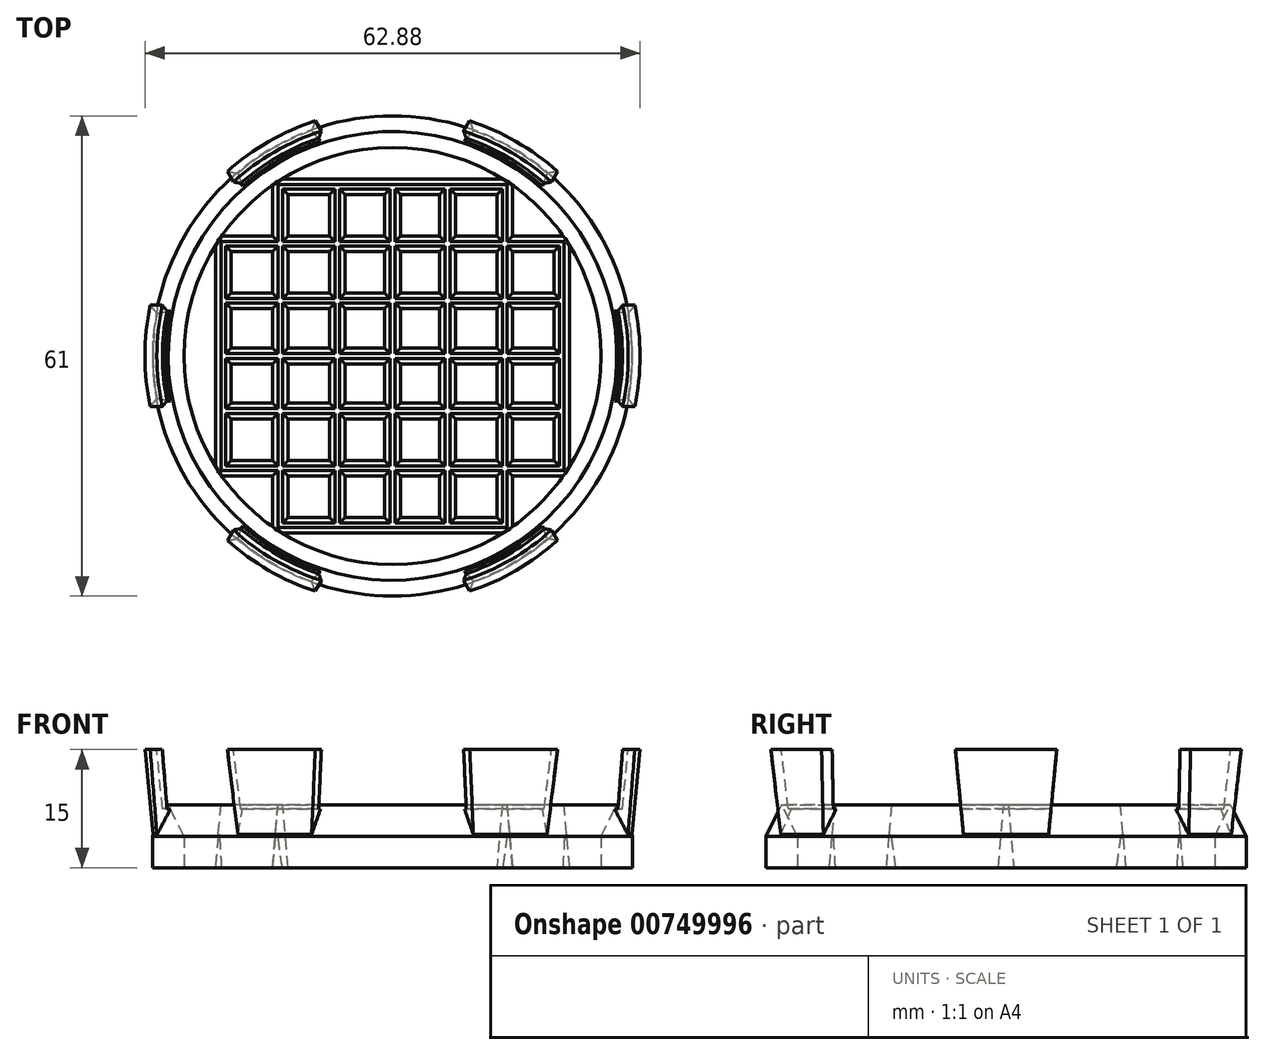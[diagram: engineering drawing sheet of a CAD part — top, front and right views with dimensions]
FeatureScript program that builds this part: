
annotation { "Feature Type Name" : "Feature", "Feature Type Description" : "" }
export const myFeature = defineFeature(function(context is Context, id is Id, definition is map)
    precondition{}
    {
        {
            var Q0;
            Q0=qCreatedBy(makeId("Front.planeOp"),FACE);
            var sketch = newSketch(context, id + "F0", { "sketchPlane" : qUnion([Q0])});
            skLineSegment(sketch, "E0", {"start": v(26.5, 0) * mm, "end": v(26.5, 4) * mm});
            skLineSegment(sketch, "E1", {"start": v(26.5, 4) * mm, "end": v(28.5, 8) * mm});
            skLineSegment(sketch, "E2", {"start": v(28.5, 8) * mm, "end": v(30.5, 4) * mm});
            skLineSegment(sketch, "E3", {"start": v(30.5, 4) * mm, "end": v(30.5, 0) * mm});
            skLineSegment(sketch, "E4", {"start": v(30.5, 0) * mm, "end": v(26.5, 0) * mm});
            skLineSegment(sketch, "E5", {"start": v(0, 0) * mm, "end": v(0, 8.18) * mm, "construction": true});
            skPoint(sketch, "E6", {"position": v(28.5, 0) * mm});
            skSolve(sketch);
        }
        {
            var Q0;
            Q0=makeQuery(id+"F0.imprint","IMPRINT",FACE,{"disambiguationData":[TD([[makeQuery(id+"F0.imprint","IMPRINT",EDGE,{"derivedFrom":sQuery(id+"F0.wireOp",EDGE,"E0")}),-1.0]])]});
            var Q1;
            Q1=sQuery(id+"F0.wireOp",EDGE,"E5");
            revolve(context, id + "F1", {"surfaceOperationType" : NewSurfaceOperationType.NEW, "entities" : qUnion([Q0]), "axis" : qUnion([Q1]), "revolveType" : RevolveType.FULL});
        }
        {
            var Q0;
            Q0=qCreatedBy(makeId("Top.planeOp"),FACE);
            var sketch = newSketch(context, id + "F2", { "sketchPlane" : qUnion([Q0])});
            skCircle(sketch, "E7.0", {"center": v(0, 0) * mm, "radius": 28.5 * mm});
            skLineSegment(sketch, "E8", {"start": v(-28.48, 1) * mm, "end": v(28.48, 1) * mm});
            skLineSegment(sketch, "E9", {"start": v(-28.48, -1) * mm, "end": v(28.48, -1) * mm});
            skLineSegment(sketch, "E10.0", {"start": v(-27.86, 6) * mm, "end": v(27.86, 6) * mm});
            skLineSegment(sketch, "E11.0", {"start": v(-27.35, 8) * mm, "end": v(27.35, 8) * mm});
            skLineSegment(sketch, "E12.0", {"start": v(-25.23, 13.25) * mm, "end": v(25.23, 13.25) * mm});
            skLineSegment(sketch, "E13.0", {"start": v(-24.08, 15.25) * mm, "end": v(24.08, 15.25) * mm});
            skLineSegment(sketch, "E14.0", {"start": v(-19.8, 20.5) * mm, "end": v(19.8, 20.5) * mm});
            skLineSegment(sketch, "E15.0", {"start": v(-17.5, 22.5) * mm, "end": v(17.5, 22.5) * mm});
            skLineSegment(sketch, "E16.0", {"start": v(-27.86, -6) * mm, "end": v(27.86, -6) * mm});
            skLineSegment(sketch, "E17.0", {"start": v(-27.35, -8) * mm, "end": v(27.35, -8) * mm});
            skLineSegment(sketch, "E18.0", {"start": v(-25.23, -13.25) * mm, "end": v(25.23, -13.25) * mm});
            skLineSegment(sketch, "E19.0", {"start": v(-24.08, -15.25) * mm, "end": v(24.08, -15.25) * mm});
            skLineSegment(sketch, "E20.0", {"start": v(-19.8, -20.5) * mm, "end": v(19.8, -20.5) * mm});
            skLineSegment(sketch, "E21.0", {"start": v(-17.5, -22.5) * mm, "end": v(17.5, -22.5) * mm});
            skLineSegment(sketch, "E22", {"start": v(-1, 28.48) * mm, "end": v(-1, -28.48) * mm});
            skLineSegment(sketch, "E23", {"start": v(1, 28.48) * mm, "end": v(1, -28.48) * mm});
            skLineSegment(sketch, "E24.0", {"start": v(-6, 27.86) * mm, "end": v(-6, -27.86) * mm});
            skLineSegment(sketch, "E25.0", {"start": v(-8, 27.35) * mm, "end": v(-8, -27.35) * mm});
            skLineSegment(sketch, "E26.0", {"start": v(-13.25, 25.23) * mm, "end": v(-13.25, -25.23) * mm});
            skLineSegment(sketch, "E27.0", {"start": v(-15.25, 24.08) * mm, "end": v(-15.25, -24.08) * mm});
            skLineSegment(sketch, "E28.0", {"start": v(-20.5, 19.8) * mm, "end": v(-20.5, -19.8) * mm});
            skLineSegment(sketch, "E29.0", {"start": v(-22.5, 17.5) * mm, "end": v(-22.5, -17.5) * mm});
            skLineSegment(sketch, "E30.0", {"start": v(8, 27.35) * mm, "end": v(8, -27.35) * mm});
            skLineSegment(sketch, "E31.0", {"start": v(6, 27.86) * mm, "end": v(6, -27.86) * mm});
            skLineSegment(sketch, "E32.0", {"start": v(13.25, 25.23) * mm, "end": v(13.25, -25.23) * mm});
            skLineSegment(sketch, "E33.0", {"start": v(15.25, 24.08) * mm, "end": v(15.25, -24.08) * mm});
            skLineSegment(sketch, "E34.0", {"start": v(20.5, 19.8) * mm, "end": v(20.5, -19.8) * mm});
            skLineSegment(sketch, "E35.0", {"start": v(22.5, 17.5) * mm, "end": v(22.5, -17.5) * mm});
            skSolve(sketch);
        }
        {
            var Q0;
            {var subQ0=sQuery(id+"F2.wireOp",EDGE,"E26.0");var subQ1=sQuery(id+"F2.wireOp",EDGE,"E7.0");var subQ2=makeQuery(id+"F2.imprint","INTERSECT",VERTEX,{"disambiguationData":[OD(0.0)],"derivedFrom":[subQ1,subQ0]});Q0=makeQuery(id+"F2.imprint","IMPRINT",FACE,{"disambiguationData":[TD([[makeQuery(id+"F2.imprint","IMPRINT",EDGE,{"disambiguationData":[TD([[subQ2,1.0]])],"derivedFrom":subQ1}),-1.0]])]});}
            var Q1;
            {var subQ0=sQuery(id+"F2.wireOp",EDGE,"E24.0");var subQ1=sQuery(id+"F2.wireOp",EDGE,"E7.0");var subQ2=makeQuery(id+"F2.imprint","INTERSECT",VERTEX,{"disambiguationData":[OD(0.0)],"derivedFrom":[subQ1,subQ0]});Q1=makeQuery(id+"F2.imprint","IMPRINT",FACE,{"disambiguationData":[TD([[makeQuery(id+"F2.imprint","IMPRINT",EDGE,{"disambiguationData":[TD([[subQ2,1.0]])],"derivedFrom":subQ1}),-1.0]])]});}
            var Q2;
            {var subQ0=sQuery(id+"F2.wireOp",EDGE,"E22");var subQ1=sQuery(id+"F2.wireOp",EDGE,"E7.0");var subQ2=makeQuery(id+"F2.imprint","INTERSECT",VERTEX,{"disambiguationData":[OD(0.0)],"derivedFrom":[subQ1,subQ0]});Q2=makeQuery(id+"F2.imprint","IMPRINT",FACE,{"disambiguationData":[TD([[makeQuery(id+"F2.imprint","IMPRINT",EDGE,{"disambiguationData":[TD([[subQ2,-1.0]])],"derivedFrom":subQ1}),-1.0]])]});}
            var Q3;
            {var subQ0=sQuery(id+"F2.wireOp",EDGE,"E30.0");var subQ1=sQuery(id+"F2.wireOp",EDGE,"E7.0");var subQ2=makeQuery(id+"F2.imprint","INTERSECT",VERTEX,{"disambiguationData":[OD(0.0)],"derivedFrom":[subQ1,subQ0]});Q3=makeQuery(id+"F2.imprint","IMPRINT",FACE,{"disambiguationData":[TD([[makeQuery(id+"F2.imprint","IMPRINT",EDGE,{"disambiguationData":[TD([[subQ2,1.0]])],"derivedFrom":subQ1}),-1.0]])]});}
            var Q4;
            {var subQ0=sQuery(id+"F2.wireOp",EDGE,"E32.0");var subQ1=sQuery(id+"F2.wireOp",EDGE,"E7.0");var subQ2=makeQuery(id+"F2.imprint","INTERSECT",VERTEX,{"disambiguationData":[OD(0.0)],"derivedFrom":[subQ1,subQ0]});Q4=makeQuery(id+"F2.imprint","IMPRINT",FACE,{"disambiguationData":[TD([[makeQuery(id+"F2.imprint","IMPRINT",EDGE,{"disambiguationData":[TD([[subQ2,-1.0]])],"derivedFrom":subQ1}),-1.0]])]});}
            var Q5;
            {var subQ0=sQuery(id+"F2.wireOp",EDGE,"E14.0");var subQ1=sQuery(id+"F2.wireOp",EDGE,"E7.0");var subQ2=makeQuery(id+"F2.imprint","INTERSECT",VERTEX,{"disambiguationData":[OD(0.0)],"derivedFrom":[subQ1,subQ0]});Q5=makeQuery(id+"F2.imprint","IMPRINT",FACE,{"disambiguationData":[TD([[makeQuery(id+"F2.imprint","IMPRINT",EDGE,{"disambiguationData":[TD([[subQ2,-1.0]])],"derivedFrom":subQ1}),-1.0]])]});}
            var Q6;
            {var subQ0=sQuery(id+"F2.wireOp",EDGE,"E27.0");var subQ1=sQuery(id+"F2.wireOp",EDGE,"E14.0");var subQ2=makeQuery(id+"F2.imprint","INTERSECT",VERTEX,{"derivedFrom":[subQ1,subQ0]});Q6=makeQuery(id+"F2.imprint","IMPRINT",FACE,{"disambiguationData":[TD([[makeQuery(id+"F2.imprint","IMPRINT",EDGE,{"disambiguationData":[TD([[subQ2,-1.0]])],"derivedFrom":subQ1}),1.0]])]});}
            var Q7;
            {var subQ0=sQuery(id+"F2.wireOp",EDGE,"E26.0");var subQ1=sQuery(id+"F2.wireOp",EDGE,"E14.0");var subQ2=makeQuery(id+"F2.imprint","INTERSECT",VERTEX,{"derivedFrom":[subQ1,subQ0]});Q7=makeQuery(id+"F2.imprint","IMPRINT",FACE,{"disambiguationData":[TD([[makeQuery(id+"F2.imprint","IMPRINT",EDGE,{"disambiguationData":[TD([[subQ2,-1.0]])],"derivedFrom":subQ1}),1.0]])]});}
            var Q8;
            {var subQ0=sQuery(id+"F2.wireOp",EDGE,"E25.0");var subQ1=sQuery(id+"F2.wireOp",EDGE,"E14.0");var subQ2=makeQuery(id+"F2.imprint","INTERSECT",VERTEX,{"derivedFrom":[subQ1,subQ0]});Q8=makeQuery(id+"F2.imprint","IMPRINT",FACE,{"disambiguationData":[TD([[makeQuery(id+"F2.imprint","IMPRINT",EDGE,{"disambiguationData":[TD([[subQ2,-1.0]])],"derivedFrom":subQ1}),1.0]])]});}
            var Q9;
            {var subQ0=sQuery(id+"F2.wireOp",EDGE,"E24.0");var subQ1=sQuery(id+"F2.wireOp",EDGE,"E14.0");var subQ2=makeQuery(id+"F2.imprint","INTERSECT",VERTEX,{"derivedFrom":[subQ1,subQ0]});Q9=makeQuery(id+"F2.imprint","IMPRINT",FACE,{"disambiguationData":[TD([[makeQuery(id+"F2.imprint","IMPRINT",EDGE,{"disambiguationData":[TD([[subQ2,-1.0]])],"derivedFrom":subQ1}),1.0]])]});}
            var Q10;
            {var subQ0=sQuery(id+"F2.wireOp",EDGE,"E22");var subQ1=sQuery(id+"F2.wireOp",EDGE,"E14.0");var subQ2=makeQuery(id+"F2.imprint","INTERSECT",VERTEX,{"derivedFrom":[subQ1,subQ0]});Q10=makeQuery(id+"F2.imprint","IMPRINT",FACE,{"disambiguationData":[TD([[makeQuery(id+"F2.imprint","IMPRINT",EDGE,{"disambiguationData":[TD([[subQ2,-1.0]])],"derivedFrom":subQ1}),1.0]])]});}
            var Q11;
            {var subQ0=sQuery(id+"F2.wireOp",EDGE,"E23");var subQ1=sQuery(id+"F2.wireOp",EDGE,"E14.0");var subQ2=makeQuery(id+"F2.imprint","INTERSECT",VERTEX,{"derivedFrom":[subQ1,subQ0]});Q11=makeQuery(id+"F2.imprint","IMPRINT",FACE,{"disambiguationData":[TD([[makeQuery(id+"F2.imprint","IMPRINT",EDGE,{"disambiguationData":[TD([[subQ2,-1.0]])],"derivedFrom":subQ1}),1.0]])]});}
            var Q12;
            {var subQ0=sQuery(id+"F2.wireOp",EDGE,"E31.0");var subQ1=sQuery(id+"F2.wireOp",EDGE,"E14.0");var subQ2=makeQuery(id+"F2.imprint","INTERSECT",VERTEX,{"derivedFrom":[subQ1,subQ0]});Q12=makeQuery(id+"F2.imprint","IMPRINT",FACE,{"disambiguationData":[TD([[makeQuery(id+"F2.imprint","IMPRINT",EDGE,{"disambiguationData":[TD([[subQ2,-1.0]])],"derivedFrom":subQ1}),1.0]])]});}
            var Q13;
            {var subQ0=sQuery(id+"F2.wireOp",EDGE,"E30.0");var subQ1=sQuery(id+"F2.wireOp",EDGE,"E14.0");var subQ2=makeQuery(id+"F2.imprint","INTERSECT",VERTEX,{"derivedFrom":[subQ1,subQ0]});Q13=makeQuery(id+"F2.imprint","IMPRINT",FACE,{"disambiguationData":[TD([[makeQuery(id+"F2.imprint","IMPRINT",EDGE,{"disambiguationData":[TD([[subQ2,-1.0]])],"derivedFrom":subQ1}),1.0]])]});}
            var Q14;
            {var subQ0=sQuery(id+"F2.wireOp",EDGE,"E32.0");var subQ1=sQuery(id+"F2.wireOp",EDGE,"E14.0");var subQ2=makeQuery(id+"F2.imprint","INTERSECT",VERTEX,{"derivedFrom":[subQ1,subQ0]});Q14=makeQuery(id+"F2.imprint","IMPRINT",FACE,{"disambiguationData":[TD([[makeQuery(id+"F2.imprint","IMPRINT",EDGE,{"disambiguationData":[TD([[subQ2,-1.0]])],"derivedFrom":subQ1}),1.0]])]});}
            var Q15;
            {var subQ0=sQuery(id+"F2.wireOp",EDGE,"E14.0");var subQ1=sQuery(id+"F2.wireOp",EDGE,"E7.0");var subQ2=makeQuery(id+"F2.imprint","INTERSECT",VERTEX,{"disambiguationData":[OD(1.0)],"derivedFrom":[subQ1,subQ0]});Q15=makeQuery(id+"F2.imprint","IMPRINT",FACE,{"disambiguationData":[TD([[makeQuery(id+"F2.imprint","IMPRINT",EDGE,{"disambiguationData":[TD([[subQ2,1.0]])],"derivedFrom":subQ1}),-1.0]])]});}
            var Q16;
            {var subQ0=sQuery(id+"F2.wireOp",EDGE,"E28.0");var subQ1=sQuery(id+"F2.wireOp",EDGE,"E7.0");var subQ2=makeQuery(id+"F2.imprint","INTERSECT",VERTEX,{"disambiguationData":[OD(0.0)],"derivedFrom":[subQ1,subQ0]});Q16=makeQuery(id+"F2.imprint","IMPRINT",FACE,{"disambiguationData":[TD([[makeQuery(id+"F2.imprint","IMPRINT",EDGE,{"disambiguationData":[TD([[subQ2,1.0]])],"derivedFrom":subQ1}),-1.0]])]});}
            var Q17;
            {var subQ0=sQuery(id+"F2.wireOp",EDGE,"E27.0");var subQ1=sQuery(id+"F2.wireOp",EDGE,"E13.0");var subQ2=makeQuery(id+"F2.imprint","INTERSECT",VERTEX,{"derivedFrom":[subQ1,subQ0]});Q17=makeQuery(id+"F2.imprint","IMPRINT",FACE,{"disambiguationData":[TD([[makeQuery(id+"F2.imprint","IMPRINT",EDGE,{"disambiguationData":[TD([[subQ2,-1.0]])],"derivedFrom":subQ1}),1.0]])]});}
            var Q18;
            {var subQ0=sQuery(id+"F2.wireOp",EDGE,"E25.0");var subQ1=sQuery(id+"F2.wireOp",EDGE,"E13.0");var subQ2=makeQuery(id+"F2.imprint","INTERSECT",VERTEX,{"derivedFrom":[subQ1,subQ0]});Q18=makeQuery(id+"F2.imprint","IMPRINT",FACE,{"disambiguationData":[TD([[makeQuery(id+"F2.imprint","IMPRINT",EDGE,{"disambiguationData":[TD([[subQ2,-1.0]])],"derivedFrom":subQ1}),1.0]])]});}
            var Q19;
            {var subQ0=sQuery(id+"F2.wireOp",EDGE,"E22");var subQ1=sQuery(id+"F2.wireOp",EDGE,"E13.0");var subQ2=makeQuery(id+"F2.imprint","INTERSECT",VERTEX,{"derivedFrom":[subQ1,subQ0]});Q19=makeQuery(id+"F2.imprint","IMPRINT",FACE,{"disambiguationData":[TD([[makeQuery(id+"F2.imprint","IMPRINT",EDGE,{"disambiguationData":[TD([[subQ2,-1.0]])],"derivedFrom":subQ1}),1.0]])]});}
            var Q20;
            {var subQ0=sQuery(id+"F2.wireOp",EDGE,"E31.0");var subQ1=sQuery(id+"F2.wireOp",EDGE,"E13.0");var subQ2=makeQuery(id+"F2.imprint","INTERSECT",VERTEX,{"derivedFrom":[subQ1,subQ0]});Q20=makeQuery(id+"F2.imprint","IMPRINT",FACE,{"disambiguationData":[TD([[makeQuery(id+"F2.imprint","IMPRINT",EDGE,{"disambiguationData":[TD([[subQ2,-1.0]])],"derivedFrom":subQ1}),1.0]])]});}
            var Q21;
            {var subQ0=sQuery(id+"F2.wireOp",EDGE,"E32.0");var subQ1=sQuery(id+"F2.wireOp",EDGE,"E13.0");var subQ2=makeQuery(id+"F2.imprint","INTERSECT",VERTEX,{"derivedFrom":[subQ1,subQ0]});Q21=makeQuery(id+"F2.imprint","IMPRINT",FACE,{"disambiguationData":[TD([[makeQuery(id+"F2.imprint","IMPRINT",EDGE,{"disambiguationData":[TD([[subQ2,-1.0]])],"derivedFrom":subQ1}),1.0]])]});}
            var Q22;
            {var subQ0=sQuery(id+"F2.wireOp",EDGE,"E34.0");var subQ1=sQuery(id+"F2.wireOp",EDGE,"E7.0");var subQ2=makeQuery(id+"F2.imprint","INTERSECT",VERTEX,{"disambiguationData":[OD(0.0)],"derivedFrom":[subQ1,subQ0]});Q22=makeQuery(id+"F2.imprint","IMPRINT",FACE,{"disambiguationData":[TD([[makeQuery(id+"F2.imprint","IMPRINT",EDGE,{"disambiguationData":[TD([[subQ2,-1.0]])],"derivedFrom":subQ1}),-1.0]])]});}
            var Q23;
            {var subQ0=sQuery(id+"F2.wireOp",EDGE,"E12.0");var subQ1=sQuery(id+"F2.wireOp",EDGE,"E7.0");var subQ2=makeQuery(id+"F2.imprint","INTERSECT",VERTEX,{"disambiguationData":[OD(0.0)],"derivedFrom":[subQ1,subQ0]});Q23=makeQuery(id+"F2.imprint","IMPRINT",FACE,{"disambiguationData":[TD([[makeQuery(id+"F2.imprint","IMPRINT",EDGE,{"disambiguationData":[TD([[subQ2,-1.0]])],"derivedFrom":subQ1}),-1.0]])]});}
            var Q24;
            {var subQ0=sQuery(id+"F2.wireOp",EDGE,"E29.0");var subQ1=sQuery(id+"F2.wireOp",EDGE,"E12.0");var subQ2=makeQuery(id+"F2.imprint","INTERSECT",VERTEX,{"derivedFrom":[subQ1,subQ0]});Q24=makeQuery(id+"F2.imprint","IMPRINT",FACE,{"disambiguationData":[TD([[makeQuery(id+"F2.imprint","IMPRINT",EDGE,{"disambiguationData":[TD([[subQ2,-1.0]])],"derivedFrom":subQ1}),1.0]])]});}
            var Q25;
            {var subQ0=sQuery(id+"F2.wireOp",EDGE,"E28.0");var subQ1=sQuery(id+"F2.wireOp",EDGE,"E12.0");var subQ2=makeQuery(id+"F2.imprint","INTERSECT",VERTEX,{"derivedFrom":[subQ1,subQ0]});Q25=makeQuery(id+"F2.imprint","IMPRINT",FACE,{"disambiguationData":[TD([[makeQuery(id+"F2.imprint","IMPRINT",EDGE,{"disambiguationData":[TD([[subQ2,-1.0]])],"derivedFrom":subQ1}),1.0]])]});}
            var Q26;
            {var subQ0=sQuery(id+"F2.wireOp",EDGE,"E27.0");var subQ1=sQuery(id+"F2.wireOp",EDGE,"E12.0");var subQ2=makeQuery(id+"F2.imprint","INTERSECT",VERTEX,{"derivedFrom":[subQ1,subQ0]});Q26=makeQuery(id+"F2.imprint","IMPRINT",FACE,{"disambiguationData":[TD([[makeQuery(id+"F2.imprint","IMPRINT",EDGE,{"disambiguationData":[TD([[subQ2,-1.0]])],"derivedFrom":subQ1}),1.0]])]});}
            var Q27;
            {var subQ0=sQuery(id+"F2.wireOp",EDGE,"E26.0");var subQ1=sQuery(id+"F2.wireOp",EDGE,"E12.0");var subQ2=makeQuery(id+"F2.imprint","INTERSECT",VERTEX,{"derivedFrom":[subQ1,subQ0]});Q27=makeQuery(id+"F2.imprint","IMPRINT",FACE,{"disambiguationData":[TD([[makeQuery(id+"F2.imprint","IMPRINT",EDGE,{"disambiguationData":[TD([[subQ2,-1.0]])],"derivedFrom":subQ1}),1.0]])]});}
            var Q28;
            {var subQ0=sQuery(id+"F2.wireOp",EDGE,"E25.0");var subQ1=sQuery(id+"F2.wireOp",EDGE,"E12.0");var subQ2=makeQuery(id+"F2.imprint","INTERSECT",VERTEX,{"derivedFrom":[subQ1,subQ0]});Q28=makeQuery(id+"F2.imprint","IMPRINT",FACE,{"disambiguationData":[TD([[makeQuery(id+"F2.imprint","IMPRINT",EDGE,{"disambiguationData":[TD([[subQ2,-1.0]])],"derivedFrom":subQ1}),1.0]])]});}
            var Q29;
            {var subQ0=sQuery(id+"F2.wireOp",EDGE,"E24.0");var subQ1=sQuery(id+"F2.wireOp",EDGE,"E12.0");var subQ2=makeQuery(id+"F2.imprint","INTERSECT",VERTEX,{"derivedFrom":[subQ1,subQ0]});Q29=makeQuery(id+"F2.imprint","IMPRINT",FACE,{"disambiguationData":[TD([[makeQuery(id+"F2.imprint","IMPRINT",EDGE,{"disambiguationData":[TD([[subQ2,-1.0]])],"derivedFrom":subQ1}),1.0]])]});}
            var Q30;
            {var subQ0=sQuery(id+"F2.wireOp",EDGE,"E22");var subQ1=sQuery(id+"F2.wireOp",EDGE,"E12.0");var subQ2=makeQuery(id+"F2.imprint","INTERSECT",VERTEX,{"derivedFrom":[subQ1,subQ0]});Q30=makeQuery(id+"F2.imprint","IMPRINT",FACE,{"disambiguationData":[TD([[makeQuery(id+"F2.imprint","IMPRINT",EDGE,{"disambiguationData":[TD([[subQ2,-1.0]])],"derivedFrom":subQ1}),1.0]])]});}
            var Q31;
            {var subQ0=sQuery(id+"F2.wireOp",EDGE,"E23");var subQ1=sQuery(id+"F2.wireOp",EDGE,"E12.0");var subQ2=makeQuery(id+"F2.imprint","INTERSECT",VERTEX,{"derivedFrom":[subQ1,subQ0]});Q31=makeQuery(id+"F2.imprint","IMPRINT",FACE,{"disambiguationData":[TD([[makeQuery(id+"F2.imprint","IMPRINT",EDGE,{"disambiguationData":[TD([[subQ2,-1.0]])],"derivedFrom":subQ1}),1.0]])]});}
            var Q32;
            {var subQ0=sQuery(id+"F2.wireOp",EDGE,"E31.0");var subQ1=sQuery(id+"F2.wireOp",EDGE,"E12.0");var subQ2=makeQuery(id+"F2.imprint","INTERSECT",VERTEX,{"derivedFrom":[subQ1,subQ0]});Q32=makeQuery(id+"F2.imprint","IMPRINT",FACE,{"disambiguationData":[TD([[makeQuery(id+"F2.imprint","IMPRINT",EDGE,{"disambiguationData":[TD([[subQ2,-1.0]])],"derivedFrom":subQ1}),1.0]])]});}
            var Q33;
            {var subQ0=sQuery(id+"F2.wireOp",EDGE,"E30.0");var subQ1=sQuery(id+"F2.wireOp",EDGE,"E12.0");var subQ2=makeQuery(id+"F2.imprint","INTERSECT",VERTEX,{"derivedFrom":[subQ1,subQ0]});Q33=makeQuery(id+"F2.imprint","IMPRINT",FACE,{"disambiguationData":[TD([[makeQuery(id+"F2.imprint","IMPRINT",EDGE,{"disambiguationData":[TD([[subQ2,-1.0]])],"derivedFrom":subQ1}),1.0]])]});}
            var Q34;
            {var subQ0=sQuery(id+"F2.wireOp",EDGE,"E32.0");var subQ1=sQuery(id+"F2.wireOp",EDGE,"E12.0");var subQ2=makeQuery(id+"F2.imprint","INTERSECT",VERTEX,{"derivedFrom":[subQ1,subQ0]});Q34=makeQuery(id+"F2.imprint","IMPRINT",FACE,{"disambiguationData":[TD([[makeQuery(id+"F2.imprint","IMPRINT",EDGE,{"disambiguationData":[TD([[subQ2,-1.0]])],"derivedFrom":subQ1}),1.0]])]});}
            var Q35;
            {var subQ0=sQuery(id+"F2.wireOp",EDGE,"E33.0");var subQ1=sQuery(id+"F2.wireOp",EDGE,"E12.0");var subQ2=makeQuery(id+"F2.imprint","INTERSECT",VERTEX,{"derivedFrom":[subQ1,subQ0]});Q35=makeQuery(id+"F2.imprint","IMPRINT",FACE,{"disambiguationData":[TD([[makeQuery(id+"F2.imprint","IMPRINT",EDGE,{"disambiguationData":[TD([[subQ2,-1.0]])],"derivedFrom":subQ1}),1.0]])]});}
            var Q36;
            {var subQ0=sQuery(id+"F2.wireOp",EDGE,"E34.0");var subQ1=sQuery(id+"F2.wireOp",EDGE,"E12.0");var subQ2=makeQuery(id+"F2.imprint","INTERSECT",VERTEX,{"derivedFrom":[subQ1,subQ0]});Q36=makeQuery(id+"F2.imprint","IMPRINT",FACE,{"disambiguationData":[TD([[makeQuery(id+"F2.imprint","IMPRINT",EDGE,{"disambiguationData":[TD([[subQ2,-1.0]])],"derivedFrom":subQ1}),1.0]])]});}
            var Q37;
            {var subQ0=sQuery(id+"F2.wireOp",EDGE,"E12.0");var subQ1=sQuery(id+"F2.wireOp",EDGE,"E7.0");var subQ2=makeQuery(id+"F2.imprint","INTERSECT",VERTEX,{"disambiguationData":[OD(1.0)],"derivedFrom":[subQ1,subQ0]});Q37=makeQuery(id+"F2.imprint","IMPRINT",FACE,{"disambiguationData":[TD([[makeQuery(id+"F2.imprint","IMPRINT",EDGE,{"disambiguationData":[TD([[subQ2,1.0]])],"derivedFrom":subQ1}),-1.0]])]});}
            var Q38;
            {var subQ0=sQuery(id+"F2.wireOp",EDGE,"E29.0");var subQ1=sQuery(id+"F2.wireOp",EDGE,"E11.0");var subQ2=makeQuery(id+"F2.imprint","INTERSECT",VERTEX,{"derivedFrom":[subQ1,subQ0]});Q38=makeQuery(id+"F2.imprint","IMPRINT",FACE,{"disambiguationData":[TD([[makeQuery(id+"F2.imprint","IMPRINT",EDGE,{"disambiguationData":[TD([[subQ2,-1.0]])],"derivedFrom":subQ1}),1.0]])]});}
            var Q39;
            {var subQ0=sQuery(id+"F2.wireOp",EDGE,"E27.0");var subQ1=sQuery(id+"F2.wireOp",EDGE,"E11.0");var subQ2=makeQuery(id+"F2.imprint","INTERSECT",VERTEX,{"derivedFrom":[subQ1,subQ0]});Q39=makeQuery(id+"F2.imprint","IMPRINT",FACE,{"disambiguationData":[TD([[makeQuery(id+"F2.imprint","IMPRINT",EDGE,{"disambiguationData":[TD([[subQ2,-1.0]])],"derivedFrom":subQ1}),1.0]])]});}
            var Q40;
            {var subQ0=sQuery(id+"F2.wireOp",EDGE,"E25.0");var subQ1=sQuery(id+"F2.wireOp",EDGE,"E11.0");var subQ2=makeQuery(id+"F2.imprint","INTERSECT",VERTEX,{"derivedFrom":[subQ1,subQ0]});Q40=makeQuery(id+"F2.imprint","IMPRINT",FACE,{"disambiguationData":[TD([[makeQuery(id+"F2.imprint","IMPRINT",EDGE,{"disambiguationData":[TD([[subQ2,-1.0]])],"derivedFrom":subQ1}),1.0]])]});}
            var Q41;
            {var subQ0=sQuery(id+"F2.wireOp",EDGE,"E22");var subQ1=sQuery(id+"F2.wireOp",EDGE,"E11.0");var subQ2=makeQuery(id+"F2.imprint","INTERSECT",VERTEX,{"derivedFrom":[subQ1,subQ0]});Q41=makeQuery(id+"F2.imprint","IMPRINT",FACE,{"disambiguationData":[TD([[makeQuery(id+"F2.imprint","IMPRINT",EDGE,{"disambiguationData":[TD([[subQ2,-1.0]])],"derivedFrom":subQ1}),1.0]])]});}
            var Q42;
            {var subQ0=sQuery(id+"F2.wireOp",EDGE,"E31.0");var subQ1=sQuery(id+"F2.wireOp",EDGE,"E11.0");var subQ2=makeQuery(id+"F2.imprint","INTERSECT",VERTEX,{"derivedFrom":[subQ1,subQ0]});Q42=makeQuery(id+"F2.imprint","IMPRINT",FACE,{"disambiguationData":[TD([[makeQuery(id+"F2.imprint","IMPRINT",EDGE,{"disambiguationData":[TD([[subQ2,-1.0]])],"derivedFrom":subQ1}),1.0]])]});}
            var Q43;
            {var subQ0=sQuery(id+"F2.wireOp",EDGE,"E32.0");var subQ1=sQuery(id+"F2.wireOp",EDGE,"E11.0");var subQ2=makeQuery(id+"F2.imprint","INTERSECT",VERTEX,{"derivedFrom":[subQ1,subQ0]});Q43=makeQuery(id+"F2.imprint","IMPRINT",FACE,{"disambiguationData":[TD([[makeQuery(id+"F2.imprint","IMPRINT",EDGE,{"disambiguationData":[TD([[subQ2,-1.0]])],"derivedFrom":subQ1}),1.0]])]});}
            var Q44;
            {var subQ0=sQuery(id+"F2.wireOp",EDGE,"E34.0");var subQ1=sQuery(id+"F2.wireOp",EDGE,"E11.0");var subQ2=makeQuery(id+"F2.imprint","INTERSECT",VERTEX,{"derivedFrom":[subQ1,subQ0]});Q44=makeQuery(id+"F2.imprint","IMPRINT",FACE,{"disambiguationData":[TD([[makeQuery(id+"F2.imprint","IMPRINT",EDGE,{"disambiguationData":[TD([[subQ2,-1.0]])],"derivedFrom":subQ1}),1.0]])]});}
            var Q45;
            {var subQ0=sQuery(id+"F2.wireOp",EDGE,"E10.0");var subQ1=sQuery(id+"F2.wireOp",EDGE,"E7.0");var subQ2=makeQuery(id+"F2.imprint","INTERSECT",VERTEX,{"disambiguationData":[OD(0.0)],"derivedFrom":[subQ1,subQ0]});Q45=makeQuery(id+"F2.imprint","IMPRINT",FACE,{"disambiguationData":[TD([[makeQuery(id+"F2.imprint","IMPRINT",EDGE,{"disambiguationData":[TD([[subQ2,-1.0]])],"derivedFrom":subQ1}),-1.0]])]});}
            var Q46;
            {var subQ0=sQuery(id+"F2.wireOp",EDGE,"E29.0");var subQ1=sQuery(id+"F2.wireOp",EDGE,"E10.0");var subQ2=makeQuery(id+"F2.imprint","INTERSECT",VERTEX,{"derivedFrom":[subQ1,subQ0]});Q46=makeQuery(id+"F2.imprint","IMPRINT",FACE,{"disambiguationData":[TD([[makeQuery(id+"F2.imprint","IMPRINT",EDGE,{"disambiguationData":[TD([[subQ2,-1.0]])],"derivedFrom":subQ1}),1.0]])]});}
            var Q47;
            {var subQ0=sQuery(id+"F2.wireOp",EDGE,"E28.0");var subQ1=sQuery(id+"F2.wireOp",EDGE,"E10.0");var subQ2=makeQuery(id+"F2.imprint","INTERSECT",VERTEX,{"derivedFrom":[subQ1,subQ0]});Q47=makeQuery(id+"F2.imprint","IMPRINT",FACE,{"disambiguationData":[TD([[makeQuery(id+"F2.imprint","IMPRINT",EDGE,{"disambiguationData":[TD([[subQ2,-1.0]])],"derivedFrom":subQ1}),1.0]])]});}
            var Q48;
            {var subQ0=sQuery(id+"F2.wireOp",EDGE,"E27.0");var subQ1=sQuery(id+"F2.wireOp",EDGE,"E10.0");var subQ2=makeQuery(id+"F2.imprint","INTERSECT",VERTEX,{"derivedFrom":[subQ1,subQ0]});Q48=makeQuery(id+"F2.imprint","IMPRINT",FACE,{"disambiguationData":[TD([[makeQuery(id+"F2.imprint","IMPRINT",EDGE,{"disambiguationData":[TD([[subQ2,-1.0]])],"derivedFrom":subQ1}),1.0]])]});}
            var Q49;
            {var subQ0=sQuery(id+"F2.wireOp",EDGE,"E26.0");var subQ1=sQuery(id+"F2.wireOp",EDGE,"E10.0");var subQ2=makeQuery(id+"F2.imprint","INTERSECT",VERTEX,{"derivedFrom":[subQ1,subQ0]});Q49=makeQuery(id+"F2.imprint","IMPRINT",FACE,{"disambiguationData":[TD([[makeQuery(id+"F2.imprint","IMPRINT",EDGE,{"disambiguationData":[TD([[subQ2,-1.0]])],"derivedFrom":subQ1}),1.0]])]});}
            var Q50;
            {var subQ0=sQuery(id+"F2.wireOp",EDGE,"E25.0");var subQ1=sQuery(id+"F2.wireOp",EDGE,"E10.0");var subQ2=makeQuery(id+"F2.imprint","INTERSECT",VERTEX,{"derivedFrom":[subQ1,subQ0]});Q50=makeQuery(id+"F2.imprint","IMPRINT",FACE,{"disambiguationData":[TD([[makeQuery(id+"F2.imprint","IMPRINT",EDGE,{"disambiguationData":[TD([[subQ2,-1.0]])],"derivedFrom":subQ1}),1.0]])]});}
            var Q51;
            {var subQ0=sQuery(id+"F2.wireOp",EDGE,"E24.0");var subQ1=sQuery(id+"F2.wireOp",EDGE,"E10.0");var subQ2=makeQuery(id+"F2.imprint","INTERSECT",VERTEX,{"derivedFrom":[subQ1,subQ0]});Q51=makeQuery(id+"F2.imprint","IMPRINT",FACE,{"disambiguationData":[TD([[makeQuery(id+"F2.imprint","IMPRINT",EDGE,{"disambiguationData":[TD([[subQ2,-1.0]])],"derivedFrom":subQ1}),1.0]])]});}
            var Q52;
            {var subQ0=sQuery(id+"F2.wireOp",EDGE,"E22");var subQ1=sQuery(id+"F2.wireOp",EDGE,"E10.0");var subQ2=makeQuery(id+"F2.imprint","INTERSECT",VERTEX,{"derivedFrom":[subQ1,subQ0]});Q52=makeQuery(id+"F2.imprint","IMPRINT",FACE,{"disambiguationData":[TD([[makeQuery(id+"F2.imprint","IMPRINT",EDGE,{"disambiguationData":[TD([[subQ2,-1.0]])],"derivedFrom":subQ1}),1.0]])]});}
            var Q53;
            {var subQ0=sQuery(id+"F2.wireOp",EDGE,"E23");var subQ1=sQuery(id+"F2.wireOp",EDGE,"E10.0");var subQ2=makeQuery(id+"F2.imprint","INTERSECT",VERTEX,{"derivedFrom":[subQ1,subQ0]});Q53=makeQuery(id+"F2.imprint","IMPRINT",FACE,{"disambiguationData":[TD([[makeQuery(id+"F2.imprint","IMPRINT",EDGE,{"disambiguationData":[TD([[subQ2,-1.0]])],"derivedFrom":subQ1}),1.0]])]});}
            var Q54;
            {var subQ0=sQuery(id+"F2.wireOp",EDGE,"E31.0");var subQ1=sQuery(id+"F2.wireOp",EDGE,"E10.0");var subQ2=makeQuery(id+"F2.imprint","INTERSECT",VERTEX,{"derivedFrom":[subQ1,subQ0]});Q54=makeQuery(id+"F2.imprint","IMPRINT",FACE,{"disambiguationData":[TD([[makeQuery(id+"F2.imprint","IMPRINT",EDGE,{"disambiguationData":[TD([[subQ2,-1.0]])],"derivedFrom":subQ1}),1.0]])]});}
            var Q55;
            {var subQ0=sQuery(id+"F2.wireOp",EDGE,"E30.0");var subQ1=sQuery(id+"F2.wireOp",EDGE,"E10.0");var subQ2=makeQuery(id+"F2.imprint","INTERSECT",VERTEX,{"derivedFrom":[subQ1,subQ0]});Q55=makeQuery(id+"F2.imprint","IMPRINT",FACE,{"disambiguationData":[TD([[makeQuery(id+"F2.imprint","IMPRINT",EDGE,{"disambiguationData":[TD([[subQ2,-1.0]])],"derivedFrom":subQ1}),1.0]])]});}
            var Q56;
            {var subQ0=sQuery(id+"F2.wireOp",EDGE,"E32.0");var subQ1=sQuery(id+"F2.wireOp",EDGE,"E10.0");var subQ2=makeQuery(id+"F2.imprint","INTERSECT",VERTEX,{"derivedFrom":[subQ1,subQ0]});Q56=makeQuery(id+"F2.imprint","IMPRINT",FACE,{"disambiguationData":[TD([[makeQuery(id+"F2.imprint","IMPRINT",EDGE,{"disambiguationData":[TD([[subQ2,-1.0]])],"derivedFrom":subQ1}),1.0]])]});}
            var Q57;
            {var subQ0=sQuery(id+"F2.wireOp",EDGE,"E33.0");var subQ1=sQuery(id+"F2.wireOp",EDGE,"E10.0");var subQ2=makeQuery(id+"F2.imprint","INTERSECT",VERTEX,{"derivedFrom":[subQ1,subQ0]});Q57=makeQuery(id+"F2.imprint","IMPRINT",FACE,{"disambiguationData":[TD([[makeQuery(id+"F2.imprint","IMPRINT",EDGE,{"disambiguationData":[TD([[subQ2,-1.0]])],"derivedFrom":subQ1}),1.0]])]});}
            var Q58;
            {var subQ0=sQuery(id+"F2.wireOp",EDGE,"E34.0");var subQ1=sQuery(id+"F2.wireOp",EDGE,"E10.0");var subQ2=makeQuery(id+"F2.imprint","INTERSECT",VERTEX,{"derivedFrom":[subQ1,subQ0]});Q58=makeQuery(id+"F2.imprint","IMPRINT",FACE,{"disambiguationData":[TD([[makeQuery(id+"F2.imprint","IMPRINT",EDGE,{"disambiguationData":[TD([[subQ2,-1.0]])],"derivedFrom":subQ1}),1.0]])]});}
            var Q59;
            {var subQ0=sQuery(id+"F2.wireOp",EDGE,"E10.0");var subQ1=sQuery(id+"F2.wireOp",EDGE,"E7.0");var subQ2=makeQuery(id+"F2.imprint","INTERSECT",VERTEX,{"disambiguationData":[OD(1.0)],"derivedFrom":[subQ1,subQ0]});Q59=makeQuery(id+"F2.imprint","IMPRINT",FACE,{"disambiguationData":[TD([[makeQuery(id+"F2.imprint","IMPRINT",EDGE,{"disambiguationData":[TD([[subQ2,1.0]])],"derivedFrom":subQ1}),-1.0]])]});}
            var Q60;
            {var subQ0=sQuery(id+"F2.wireOp",EDGE,"E29.0");var subQ1=sQuery(id+"F2.wireOp",EDGE,"E8");var subQ2=makeQuery(id+"F2.imprint","INTERSECT",VERTEX,{"derivedFrom":[subQ1,subQ0]});Q60=makeQuery(id+"F2.imprint","IMPRINT",FACE,{"disambiguationData":[TD([[makeQuery(id+"F2.imprint","IMPRINT",EDGE,{"disambiguationData":[TD([[subQ2,-1.0]])],"derivedFrom":subQ1}),1.0]])]});}
            var Q61;
            {var subQ0=sQuery(id+"F2.wireOp",EDGE,"E27.0");var subQ1=sQuery(id+"F2.wireOp",EDGE,"E8");var subQ2=makeQuery(id+"F2.imprint","INTERSECT",VERTEX,{"derivedFrom":[subQ1,subQ0]});Q61=makeQuery(id+"F2.imprint","IMPRINT",FACE,{"disambiguationData":[TD([[makeQuery(id+"F2.imprint","IMPRINT",EDGE,{"disambiguationData":[TD([[subQ2,-1.0]])],"derivedFrom":subQ1}),1.0]])]});}
            var Q62;
            {var subQ0=sQuery(id+"F2.wireOp",EDGE,"E25.0");var subQ1=sQuery(id+"F2.wireOp",EDGE,"E8");var subQ2=makeQuery(id+"F2.imprint","INTERSECT",VERTEX,{"derivedFrom":[subQ1,subQ0]});Q62=makeQuery(id+"F2.imprint","IMPRINT",FACE,{"disambiguationData":[TD([[makeQuery(id+"F2.imprint","IMPRINT",EDGE,{"disambiguationData":[TD([[subQ2,-1.0]])],"derivedFrom":subQ1}),1.0]])]});}
            var Q63;
            {var subQ0=sQuery(id+"F2.wireOp",EDGE,"E22");var subQ1=sQuery(id+"F2.wireOp",EDGE,"E8");var subQ2=makeQuery(id+"F2.imprint","INTERSECT",VERTEX,{"derivedFrom":[subQ1,subQ0]});Q63=makeQuery(id+"F2.imprint","IMPRINT",FACE,{"disambiguationData":[TD([[makeQuery(id+"F2.imprint","IMPRINT",EDGE,{"disambiguationData":[TD([[subQ2,-1.0]])],"derivedFrom":subQ1}),1.0]])]});}
            var Q64;
            {var subQ0=sQuery(id+"F2.wireOp",EDGE,"E31.0");var subQ1=sQuery(id+"F2.wireOp",EDGE,"E8");var subQ2=makeQuery(id+"F2.imprint","INTERSECT",VERTEX,{"derivedFrom":[subQ1,subQ0]});Q64=makeQuery(id+"F2.imprint","IMPRINT",FACE,{"disambiguationData":[TD([[makeQuery(id+"F2.imprint","IMPRINT",EDGE,{"disambiguationData":[TD([[subQ2,-1.0]])],"derivedFrom":subQ1}),1.0]])]});}
            var Q65;
            {var subQ0=sQuery(id+"F2.wireOp",EDGE,"E32.0");var subQ1=sQuery(id+"F2.wireOp",EDGE,"E8");var subQ2=makeQuery(id+"F2.imprint","INTERSECT",VERTEX,{"derivedFrom":[subQ1,subQ0]});Q65=makeQuery(id+"F2.imprint","IMPRINT",FACE,{"disambiguationData":[TD([[makeQuery(id+"F2.imprint","IMPRINT",EDGE,{"disambiguationData":[TD([[subQ2,-1.0]])],"derivedFrom":subQ1}),1.0]])]});}
            var Q66;
            {var subQ0=sQuery(id+"F2.wireOp",EDGE,"E34.0");var subQ1=sQuery(id+"F2.wireOp",EDGE,"E8");var subQ2=makeQuery(id+"F2.imprint","INTERSECT",VERTEX,{"derivedFrom":[subQ1,subQ0]});Q66=makeQuery(id+"F2.imprint","IMPRINT",FACE,{"disambiguationData":[TD([[makeQuery(id+"F2.imprint","IMPRINT",EDGE,{"disambiguationData":[TD([[subQ2,-1.0]])],"derivedFrom":subQ1}),1.0]])]});}
            var Q67;
            {var subQ0=sQuery(id+"F2.wireOp",EDGE,"E8");var subQ1=sQuery(id+"F2.wireOp",EDGE,"E7.0");var subQ2=makeQuery(id+"F2.imprint","INTERSECT",VERTEX,{"disambiguationData":[OD(0.0)],"derivedFrom":[subQ1,subQ0]});Q67=makeQuery(id+"F2.imprint","IMPRINT",FACE,{"disambiguationData":[TD([[makeQuery(id+"F2.imprint","IMPRINT",EDGE,{"disambiguationData":[TD([[subQ2,1.0]])],"derivedFrom":subQ1}),-1.0]])]});}
            var Q68;
            {var subQ0=sQuery(id+"F2.wireOp",EDGE,"E29.0");var subQ1=sQuery(id+"F2.wireOp",EDGE,"E8");var subQ2=makeQuery(id+"F2.imprint","INTERSECT",VERTEX,{"derivedFrom":[subQ1,subQ0]});Q68=makeQuery(id+"F2.imprint","IMPRINT",FACE,{"disambiguationData":[TD([[makeQuery(id+"F2.imprint","IMPRINT",EDGE,{"disambiguationData":[TD([[subQ2,-1.0]])],"derivedFrom":subQ1}),-1.0]])]});}
            var Q69;
            {var subQ0=sQuery(id+"F2.wireOp",EDGE,"E28.0");var subQ1=sQuery(id+"F2.wireOp",EDGE,"E8");var subQ2=makeQuery(id+"F2.imprint","INTERSECT",VERTEX,{"derivedFrom":[subQ1,subQ0]});Q69=makeQuery(id+"F2.imprint","IMPRINT",FACE,{"disambiguationData":[TD([[makeQuery(id+"F2.imprint","IMPRINT",EDGE,{"disambiguationData":[TD([[subQ2,-1.0]])],"derivedFrom":subQ1}),-1.0]])]});}
            var Q70;
            {var subQ0=sQuery(id+"F2.wireOp",EDGE,"E27.0");var subQ1=sQuery(id+"F2.wireOp",EDGE,"E8");var subQ2=makeQuery(id+"F2.imprint","INTERSECT",VERTEX,{"derivedFrom":[subQ1,subQ0]});Q70=makeQuery(id+"F2.imprint","IMPRINT",FACE,{"disambiguationData":[TD([[makeQuery(id+"F2.imprint","IMPRINT",EDGE,{"disambiguationData":[TD([[subQ2,-1.0]])],"derivedFrom":subQ1}),-1.0]])]});}
            var Q71;
            {var subQ0=sQuery(id+"F2.wireOp",EDGE,"E26.0");var subQ1=sQuery(id+"F2.wireOp",EDGE,"E8");var subQ2=makeQuery(id+"F2.imprint","INTERSECT",VERTEX,{"derivedFrom":[subQ1,subQ0]});Q71=makeQuery(id+"F2.imprint","IMPRINT",FACE,{"disambiguationData":[TD([[makeQuery(id+"F2.imprint","IMPRINT",EDGE,{"disambiguationData":[TD([[subQ2,-1.0]])],"derivedFrom":subQ1}),-1.0]])]});}
            var Q72;
            {var subQ0=sQuery(id+"F2.wireOp",EDGE,"E25.0");var subQ1=sQuery(id+"F2.wireOp",EDGE,"E8");var subQ2=makeQuery(id+"F2.imprint","INTERSECT",VERTEX,{"derivedFrom":[subQ1,subQ0]});Q72=makeQuery(id+"F2.imprint","IMPRINT",FACE,{"disambiguationData":[TD([[makeQuery(id+"F2.imprint","IMPRINT",EDGE,{"disambiguationData":[TD([[subQ2,-1.0]])],"derivedFrom":subQ1}),-1.0]])]});}
            var Q73;
            {var subQ0=sQuery(id+"F2.wireOp",EDGE,"E24.0");var subQ1=sQuery(id+"F2.wireOp",EDGE,"E8");var subQ2=makeQuery(id+"F2.imprint","INTERSECT",VERTEX,{"derivedFrom":[subQ1,subQ0]});Q73=makeQuery(id+"F2.imprint","IMPRINT",FACE,{"disambiguationData":[TD([[makeQuery(id+"F2.imprint","IMPRINT",EDGE,{"disambiguationData":[TD([[subQ2,-1.0]])],"derivedFrom":subQ1}),-1.0]])]});}
            var Q74;
            {var subQ0=sQuery(id+"F2.wireOp",EDGE,"E22");var subQ1=sQuery(id+"F2.wireOp",EDGE,"E8");var subQ2=makeQuery(id+"F2.imprint","INTERSECT",VERTEX,{"derivedFrom":[subQ1,subQ0]});Q74=makeQuery(id+"F2.imprint","IMPRINT",FACE,{"disambiguationData":[TD([[makeQuery(id+"F2.imprint","IMPRINT",EDGE,{"disambiguationData":[TD([[subQ2,-1.0]])],"derivedFrom":subQ1}),-1.0]])]});}
            var Q75;
            {var subQ0=sQuery(id+"F2.wireOp",EDGE,"E23");var subQ1=sQuery(id+"F2.wireOp",EDGE,"E8");var subQ2=makeQuery(id+"F2.imprint","INTERSECT",VERTEX,{"derivedFrom":[subQ1,subQ0]});Q75=makeQuery(id+"F2.imprint","IMPRINT",FACE,{"disambiguationData":[TD([[makeQuery(id+"F2.imprint","IMPRINT",EDGE,{"disambiguationData":[TD([[subQ2,-1.0]])],"derivedFrom":subQ1}),-1.0]])]});}
            var Q76;
            {var subQ0=sQuery(id+"F2.wireOp",EDGE,"E31.0");var subQ1=sQuery(id+"F2.wireOp",EDGE,"E8");var subQ2=makeQuery(id+"F2.imprint","INTERSECT",VERTEX,{"derivedFrom":[subQ1,subQ0]});Q76=makeQuery(id+"F2.imprint","IMPRINT",FACE,{"disambiguationData":[TD([[makeQuery(id+"F2.imprint","IMPRINT",EDGE,{"disambiguationData":[TD([[subQ2,-1.0]])],"derivedFrom":subQ1}),-1.0]])]});}
            var Q77;
            {var subQ0=sQuery(id+"F2.wireOp",EDGE,"E30.0");var subQ1=sQuery(id+"F2.wireOp",EDGE,"E8");var subQ2=makeQuery(id+"F2.imprint","INTERSECT",VERTEX,{"derivedFrom":[subQ1,subQ0]});Q77=makeQuery(id+"F2.imprint","IMPRINT",FACE,{"disambiguationData":[TD([[makeQuery(id+"F2.imprint","IMPRINT",EDGE,{"disambiguationData":[TD([[subQ2,-1.0]])],"derivedFrom":subQ1}),-1.0]])]});}
            var Q78;
            {var subQ0=sQuery(id+"F2.wireOp",EDGE,"E32.0");var subQ1=sQuery(id+"F2.wireOp",EDGE,"E8");var subQ2=makeQuery(id+"F2.imprint","INTERSECT",VERTEX,{"derivedFrom":[subQ1,subQ0]});Q78=makeQuery(id+"F2.imprint","IMPRINT",FACE,{"disambiguationData":[TD([[makeQuery(id+"F2.imprint","IMPRINT",EDGE,{"disambiguationData":[TD([[subQ2,-1.0]])],"derivedFrom":subQ1}),-1.0]])]});}
            var Q79;
            {var subQ0=sQuery(id+"F2.wireOp",EDGE,"E33.0");var subQ1=sQuery(id+"F2.wireOp",EDGE,"E8");var subQ2=makeQuery(id+"F2.imprint","INTERSECT",VERTEX,{"derivedFrom":[subQ1,subQ0]});Q79=makeQuery(id+"F2.imprint","IMPRINT",FACE,{"disambiguationData":[TD([[makeQuery(id+"F2.imprint","IMPRINT",EDGE,{"disambiguationData":[TD([[subQ2,-1.0]])],"derivedFrom":subQ1}),-1.0]])]});}
            var Q80;
            {var subQ0=sQuery(id+"F2.wireOp",EDGE,"E34.0");var subQ1=sQuery(id+"F2.wireOp",EDGE,"E8");var subQ2=makeQuery(id+"F2.imprint","INTERSECT",VERTEX,{"derivedFrom":[subQ1,subQ0]});Q80=makeQuery(id+"F2.imprint","IMPRINT",FACE,{"disambiguationData":[TD([[makeQuery(id+"F2.imprint","IMPRINT",EDGE,{"disambiguationData":[TD([[subQ2,-1.0]])],"derivedFrom":subQ1}),-1.0]])]});}
            var Q81;
            {var subQ0=sQuery(id+"F2.wireOp",EDGE,"E8");var subQ1=sQuery(id+"F2.wireOp",EDGE,"E7.0");var subQ2=makeQuery(id+"F2.imprint","INTERSECT",VERTEX,{"disambiguationData":[OD(1.0)],"derivedFrom":[subQ1,subQ0]});Q81=makeQuery(id+"F2.imprint","IMPRINT",FACE,{"disambiguationData":[TD([[makeQuery(id+"F2.imprint","IMPRINT",EDGE,{"disambiguationData":[TD([[subQ2,-1.0]])],"derivedFrom":subQ1}),-1.0]])]});}
            var Q82;
            {var subQ0=sQuery(id+"F2.wireOp",EDGE,"E29.0");var subQ1=sQuery(id+"F2.wireOp",EDGE,"E9");var subQ2=makeQuery(id+"F2.imprint","INTERSECT",VERTEX,{"derivedFrom":[subQ1,subQ0]});Q82=makeQuery(id+"F2.imprint","IMPRINT",FACE,{"disambiguationData":[TD([[makeQuery(id+"F2.imprint","IMPRINT",EDGE,{"disambiguationData":[TD([[subQ2,-1.0]])],"derivedFrom":subQ1}),-1.0]])]});}
            var Q83;
            {var subQ0=sQuery(id+"F2.wireOp",EDGE,"E27.0");var subQ1=sQuery(id+"F2.wireOp",EDGE,"E9");var subQ2=makeQuery(id+"F2.imprint","INTERSECT",VERTEX,{"derivedFrom":[subQ1,subQ0]});Q83=makeQuery(id+"F2.imprint","IMPRINT",FACE,{"disambiguationData":[TD([[makeQuery(id+"F2.imprint","IMPRINT",EDGE,{"disambiguationData":[TD([[subQ2,-1.0]])],"derivedFrom":subQ1}),-1.0]])]});}
            var Q84;
            {var subQ0=sQuery(id+"F2.wireOp",EDGE,"E22");var subQ1=sQuery(id+"F2.wireOp",EDGE,"E9");var subQ2=makeQuery(id+"F2.imprint","INTERSECT",VERTEX,{"derivedFrom":[subQ1,subQ0]});Q84=makeQuery(id+"F2.imprint","IMPRINT",FACE,{"disambiguationData":[TD([[makeQuery(id+"F2.imprint","IMPRINT",EDGE,{"disambiguationData":[TD([[subQ2,-1.0]])],"derivedFrom":subQ1}),-1.0]])]});}
            var Q85;
            {var subQ0=sQuery(id+"F2.wireOp",EDGE,"E31.0");var subQ1=sQuery(id+"F2.wireOp",EDGE,"E9");var subQ2=makeQuery(id+"F2.imprint","INTERSECT",VERTEX,{"derivedFrom":[subQ1,subQ0]});Q85=makeQuery(id+"F2.imprint","IMPRINT",FACE,{"disambiguationData":[TD([[makeQuery(id+"F2.imprint","IMPRINT",EDGE,{"disambiguationData":[TD([[subQ2,-1.0]])],"derivedFrom":subQ1}),-1.0]])]});}
            var Q86;
            {var subQ0=sQuery(id+"F2.wireOp",EDGE,"E32.0");var subQ1=sQuery(id+"F2.wireOp",EDGE,"E9");var subQ2=makeQuery(id+"F2.imprint","INTERSECT",VERTEX,{"derivedFrom":[subQ1,subQ0]});Q86=makeQuery(id+"F2.imprint","IMPRINT",FACE,{"disambiguationData":[TD([[makeQuery(id+"F2.imprint","IMPRINT",EDGE,{"disambiguationData":[TD([[subQ2,-1.0]])],"derivedFrom":subQ1}),-1.0]])]});}
            var Q87;
            {var subQ0=sQuery(id+"F2.wireOp",EDGE,"E34.0");var subQ1=sQuery(id+"F2.wireOp",EDGE,"E9");var subQ2=makeQuery(id+"F2.imprint","INTERSECT",VERTEX,{"derivedFrom":[subQ1,subQ0]});Q87=makeQuery(id+"F2.imprint","IMPRINT",FACE,{"disambiguationData":[TD([[makeQuery(id+"F2.imprint","IMPRINT",EDGE,{"disambiguationData":[TD([[subQ2,-1.0]])],"derivedFrom":subQ1}),-1.0]])]});}
            var Q88;
            {var subQ0=sQuery(id+"F2.wireOp",EDGE,"E25.0");var subQ1=sQuery(id+"F2.wireOp",EDGE,"E9");var subQ2=makeQuery(id+"F2.imprint","INTERSECT",VERTEX,{"derivedFrom":[subQ1,subQ0]});Q88=makeQuery(id+"F2.imprint","IMPRINT",FACE,{"disambiguationData":[TD([[makeQuery(id+"F2.imprint","IMPRINT",EDGE,{"disambiguationData":[TD([[subQ2,-1.0]])],"derivedFrom":subQ1}),-1.0]])]});}
            var Q89;
            {var subQ0=sQuery(id+"F2.wireOp",EDGE,"E16.0");var subQ1=sQuery(id+"F2.wireOp",EDGE,"E7.0");var subQ2=makeQuery(id+"F2.imprint","INTERSECT",VERTEX,{"disambiguationData":[OD(0.0)],"derivedFrom":[subQ1,subQ0]});Q89=makeQuery(id+"F2.imprint","IMPRINT",FACE,{"disambiguationData":[TD([[makeQuery(id+"F2.imprint","IMPRINT",EDGE,{"disambiguationData":[TD([[subQ2,1.0]])],"derivedFrom":subQ1}),-1.0]])]});}
            var Q90;
            {var subQ0=sQuery(id+"F2.wireOp",EDGE,"E29.0");var subQ1=sQuery(id+"F2.wireOp",EDGE,"E16.0");var subQ2=makeQuery(id+"F2.imprint","INTERSECT",VERTEX,{"derivedFrom":[subQ1,subQ0]});Q90=makeQuery(id+"F2.imprint","IMPRINT",FACE,{"disambiguationData":[TD([[makeQuery(id+"F2.imprint","IMPRINT",EDGE,{"disambiguationData":[TD([[subQ2,-1.0]])],"derivedFrom":subQ1}),-1.0]])]});}
            var Q91;
            {var subQ0=sQuery(id+"F2.wireOp",EDGE,"E28.0");var subQ1=sQuery(id+"F2.wireOp",EDGE,"E16.0");var subQ2=makeQuery(id+"F2.imprint","INTERSECT",VERTEX,{"derivedFrom":[subQ1,subQ0]});Q91=makeQuery(id+"F2.imprint","IMPRINT",FACE,{"disambiguationData":[TD([[makeQuery(id+"F2.imprint","IMPRINT",EDGE,{"disambiguationData":[TD([[subQ2,-1.0]])],"derivedFrom":subQ1}),-1.0]])]});}
            var Q92;
            {var subQ0=sQuery(id+"F2.wireOp",EDGE,"E27.0");var subQ1=sQuery(id+"F2.wireOp",EDGE,"E16.0");var subQ2=makeQuery(id+"F2.imprint","INTERSECT",VERTEX,{"derivedFrom":[subQ1,subQ0]});Q92=makeQuery(id+"F2.imprint","IMPRINT",FACE,{"disambiguationData":[TD([[makeQuery(id+"F2.imprint","IMPRINT",EDGE,{"disambiguationData":[TD([[subQ2,-1.0]])],"derivedFrom":subQ1}),-1.0]])]});}
            var Q93;
            {var subQ0=sQuery(id+"F2.wireOp",EDGE,"E26.0");var subQ1=sQuery(id+"F2.wireOp",EDGE,"E16.0");var subQ2=makeQuery(id+"F2.imprint","INTERSECT",VERTEX,{"derivedFrom":[subQ1,subQ0]});Q93=makeQuery(id+"F2.imprint","IMPRINT",FACE,{"disambiguationData":[TD([[makeQuery(id+"F2.imprint","IMPRINT",EDGE,{"disambiguationData":[TD([[subQ2,-1.0]])],"derivedFrom":subQ1}),-1.0]])]});}
            var Q94;
            {var subQ0=sQuery(id+"F2.wireOp",EDGE,"E25.0");var subQ1=sQuery(id+"F2.wireOp",EDGE,"E16.0");var subQ2=makeQuery(id+"F2.imprint","INTERSECT",VERTEX,{"derivedFrom":[subQ1,subQ0]});Q94=makeQuery(id+"F2.imprint","IMPRINT",FACE,{"disambiguationData":[TD([[makeQuery(id+"F2.imprint","IMPRINT",EDGE,{"disambiguationData":[TD([[subQ2,-1.0]])],"derivedFrom":subQ1}),-1.0]])]});}
            var Q95;
            {var subQ0=sQuery(id+"F2.wireOp",EDGE,"E24.0");var subQ1=sQuery(id+"F2.wireOp",EDGE,"E16.0");var subQ2=makeQuery(id+"F2.imprint","INTERSECT",VERTEX,{"derivedFrom":[subQ1,subQ0]});Q95=makeQuery(id+"F2.imprint","IMPRINT",FACE,{"disambiguationData":[TD([[makeQuery(id+"F2.imprint","IMPRINT",EDGE,{"disambiguationData":[TD([[subQ2,-1.0]])],"derivedFrom":subQ1}),-1.0]])]});}
            var Q96;
            {var subQ0=sQuery(id+"F2.wireOp",EDGE,"E22");var subQ1=sQuery(id+"F2.wireOp",EDGE,"E16.0");var subQ2=makeQuery(id+"F2.imprint","INTERSECT",VERTEX,{"derivedFrom":[subQ1,subQ0]});Q96=makeQuery(id+"F2.imprint","IMPRINT",FACE,{"disambiguationData":[TD([[makeQuery(id+"F2.imprint","IMPRINT",EDGE,{"disambiguationData":[TD([[subQ2,-1.0]])],"derivedFrom":subQ1}),-1.0]])]});}
            var Q97;
            {var subQ0=sQuery(id+"F2.wireOp",EDGE,"E23");var subQ1=sQuery(id+"F2.wireOp",EDGE,"E16.0");var subQ2=makeQuery(id+"F2.imprint","INTERSECT",VERTEX,{"derivedFrom":[subQ1,subQ0]});Q97=makeQuery(id+"F2.imprint","IMPRINT",FACE,{"disambiguationData":[TD([[makeQuery(id+"F2.imprint","IMPRINT",EDGE,{"disambiguationData":[TD([[subQ2,-1.0]])],"derivedFrom":subQ1}),-1.0]])]});}
            var Q98;
            {var subQ0=sQuery(id+"F2.wireOp",EDGE,"E31.0");var subQ1=sQuery(id+"F2.wireOp",EDGE,"E16.0");var subQ2=makeQuery(id+"F2.imprint","INTERSECT",VERTEX,{"derivedFrom":[subQ1,subQ0]});Q98=makeQuery(id+"F2.imprint","IMPRINT",FACE,{"disambiguationData":[TD([[makeQuery(id+"F2.imprint","IMPRINT",EDGE,{"disambiguationData":[TD([[subQ2,-1.0]])],"derivedFrom":subQ1}),-1.0]])]});}
            var Q99;
            {var subQ0=sQuery(id+"F2.wireOp",EDGE,"E30.0");var subQ1=sQuery(id+"F2.wireOp",EDGE,"E16.0");var subQ2=makeQuery(id+"F2.imprint","INTERSECT",VERTEX,{"derivedFrom":[subQ1,subQ0]});Q99=makeQuery(id+"F2.imprint","IMPRINT",FACE,{"disambiguationData":[TD([[makeQuery(id+"F2.imprint","IMPRINT",EDGE,{"disambiguationData":[TD([[subQ2,-1.0]])],"derivedFrom":subQ1}),-1.0]])]});}
            var Q100;
            {var subQ0=sQuery(id+"F2.wireOp",EDGE,"E32.0");var subQ1=sQuery(id+"F2.wireOp",EDGE,"E16.0");var subQ2=makeQuery(id+"F2.imprint","INTERSECT",VERTEX,{"derivedFrom":[subQ1,subQ0]});Q100=makeQuery(id+"F2.imprint","IMPRINT",FACE,{"disambiguationData":[TD([[makeQuery(id+"F2.imprint","IMPRINT",EDGE,{"disambiguationData":[TD([[subQ2,-1.0]])],"derivedFrom":subQ1}),-1.0]])]});}
            var Q101;
            {var subQ0=sQuery(id+"F2.wireOp",EDGE,"E33.0");var subQ1=sQuery(id+"F2.wireOp",EDGE,"E16.0");var subQ2=makeQuery(id+"F2.imprint","INTERSECT",VERTEX,{"derivedFrom":[subQ1,subQ0]});Q101=makeQuery(id+"F2.imprint","IMPRINT",FACE,{"disambiguationData":[TD([[makeQuery(id+"F2.imprint","IMPRINT",EDGE,{"disambiguationData":[TD([[subQ2,-1.0]])],"derivedFrom":subQ1}),-1.0]])]});}
            var Q102;
            {var subQ0=sQuery(id+"F2.wireOp",EDGE,"E34.0");var subQ1=sQuery(id+"F2.wireOp",EDGE,"E16.0");var subQ2=makeQuery(id+"F2.imprint","INTERSECT",VERTEX,{"derivedFrom":[subQ1,subQ0]});Q102=makeQuery(id+"F2.imprint","IMPRINT",FACE,{"disambiguationData":[TD([[makeQuery(id+"F2.imprint","IMPRINT",EDGE,{"disambiguationData":[TD([[subQ2,-1.0]])],"derivedFrom":subQ1}),-1.0]])]});}
            var Q103;
            {var subQ0=sQuery(id+"F2.wireOp",EDGE,"E16.0");var subQ1=sQuery(id+"F2.wireOp",EDGE,"E7.0");var subQ2=makeQuery(id+"F2.imprint","INTERSECT",VERTEX,{"disambiguationData":[OD(1.0)],"derivedFrom":[subQ1,subQ0]});Q103=makeQuery(id+"F2.imprint","IMPRINT",FACE,{"disambiguationData":[TD([[makeQuery(id+"F2.imprint","IMPRINT",EDGE,{"disambiguationData":[TD([[subQ2,-1.0]])],"derivedFrom":subQ1}),-1.0]])]});}
            var Q104;
            {var subQ0=sQuery(id+"F2.wireOp",EDGE,"E27.0");var subQ1=sQuery(id+"F2.wireOp",EDGE,"E17.0");var subQ2=makeQuery(id+"F2.imprint","INTERSECT",VERTEX,{"derivedFrom":[subQ1,subQ0]});Q104=makeQuery(id+"F2.imprint","IMPRINT",FACE,{"disambiguationData":[TD([[makeQuery(id+"F2.imprint","IMPRINT",EDGE,{"disambiguationData":[TD([[subQ2,-1.0]])],"derivedFrom":subQ1}),-1.0]])]});}
            var Q105;
            {var subQ0=sQuery(id+"F2.wireOp",EDGE,"E25.0");var subQ1=sQuery(id+"F2.wireOp",EDGE,"E17.0");var subQ2=makeQuery(id+"F2.imprint","INTERSECT",VERTEX,{"derivedFrom":[subQ1,subQ0]});Q105=makeQuery(id+"F2.imprint","IMPRINT",FACE,{"disambiguationData":[TD([[makeQuery(id+"F2.imprint","IMPRINT",EDGE,{"disambiguationData":[TD([[subQ2,-1.0]])],"derivedFrom":subQ1}),-1.0]])]});}
            var Q106;
            {var subQ0=sQuery(id+"F2.wireOp",EDGE,"E22");var subQ1=sQuery(id+"F2.wireOp",EDGE,"E17.0");var subQ2=makeQuery(id+"F2.imprint","INTERSECT",VERTEX,{"derivedFrom":[subQ1,subQ0]});Q106=makeQuery(id+"F2.imprint","IMPRINT",FACE,{"disambiguationData":[TD([[makeQuery(id+"F2.imprint","IMPRINT",EDGE,{"disambiguationData":[TD([[subQ2,-1.0]])],"derivedFrom":subQ1}),-1.0]])]});}
            var Q107;
            {var subQ0=sQuery(id+"F2.wireOp",EDGE,"E29.0");var subQ1=sQuery(id+"F2.wireOp",EDGE,"E17.0");var subQ2=makeQuery(id+"F2.imprint","INTERSECT",VERTEX,{"derivedFrom":[subQ1,subQ0]});Q107=makeQuery(id+"F2.imprint","IMPRINT",FACE,{"disambiguationData":[TD([[makeQuery(id+"F2.imprint","IMPRINT",EDGE,{"disambiguationData":[TD([[subQ2,-1.0]])],"derivedFrom":subQ1}),-1.0]])]});}
            var Q108;
            {var subQ0=sQuery(id+"F2.wireOp",EDGE,"E31.0");var subQ1=sQuery(id+"F2.wireOp",EDGE,"E17.0");var subQ2=makeQuery(id+"F2.imprint","INTERSECT",VERTEX,{"derivedFrom":[subQ1,subQ0]});Q108=makeQuery(id+"F2.imprint","IMPRINT",FACE,{"disambiguationData":[TD([[makeQuery(id+"F2.imprint","IMPRINT",EDGE,{"disambiguationData":[TD([[subQ2,-1.0]])],"derivedFrom":subQ1}),-1.0]])]});}
            var Q109;
            {var subQ0=sQuery(id+"F2.wireOp",EDGE,"E32.0");var subQ1=sQuery(id+"F2.wireOp",EDGE,"E17.0");var subQ2=makeQuery(id+"F2.imprint","INTERSECT",VERTEX,{"derivedFrom":[subQ1,subQ0]});Q109=makeQuery(id+"F2.imprint","IMPRINT",FACE,{"disambiguationData":[TD([[makeQuery(id+"F2.imprint","IMPRINT",EDGE,{"disambiguationData":[TD([[subQ2,-1.0]])],"derivedFrom":subQ1}),-1.0]])]});}
            var Q110;
            {var subQ0=sQuery(id+"F2.wireOp",EDGE,"E34.0");var subQ1=sQuery(id+"F2.wireOp",EDGE,"E17.0");var subQ2=makeQuery(id+"F2.imprint","INTERSECT",VERTEX,{"derivedFrom":[subQ1,subQ0]});Q110=makeQuery(id+"F2.imprint","IMPRINT",FACE,{"disambiguationData":[TD([[makeQuery(id+"F2.imprint","IMPRINT",EDGE,{"disambiguationData":[TD([[subQ2,-1.0]])],"derivedFrom":subQ1}),-1.0]])]});}
            var Q111;
            {var subQ0=sQuery(id+"F2.wireOp",EDGE,"E18.0");var subQ1=sQuery(id+"F2.wireOp",EDGE,"E7.0");var subQ2=makeQuery(id+"F2.imprint","INTERSECT",VERTEX,{"disambiguationData":[OD(0.0)],"derivedFrom":[subQ1,subQ0]});Q111=makeQuery(id+"F2.imprint","IMPRINT",FACE,{"disambiguationData":[TD([[makeQuery(id+"F2.imprint","IMPRINT",EDGE,{"disambiguationData":[TD([[subQ2,1.0]])],"derivedFrom":subQ1}),-1.0]])]});}
            var Q112;
            {var subQ0=sQuery(id+"F2.wireOp",EDGE,"E29.0");var subQ1=sQuery(id+"F2.wireOp",EDGE,"E18.0");var subQ2=makeQuery(id+"F2.imprint","INTERSECT",VERTEX,{"derivedFrom":[subQ1,subQ0]});Q112=makeQuery(id+"F2.imprint","IMPRINT",FACE,{"disambiguationData":[TD([[makeQuery(id+"F2.imprint","IMPRINT",EDGE,{"disambiguationData":[TD([[subQ2,-1.0]])],"derivedFrom":subQ1}),-1.0]])]});}
            var Q113;
            {var subQ0=sQuery(id+"F2.wireOp",EDGE,"E28.0");var subQ1=sQuery(id+"F2.wireOp",EDGE,"E18.0");var subQ2=makeQuery(id+"F2.imprint","INTERSECT",VERTEX,{"derivedFrom":[subQ1,subQ0]});Q113=makeQuery(id+"F2.imprint","IMPRINT",FACE,{"disambiguationData":[TD([[makeQuery(id+"F2.imprint","IMPRINT",EDGE,{"disambiguationData":[TD([[subQ2,-1.0]])],"derivedFrom":subQ1}),-1.0]])]});}
            var Q114;
            {var subQ0=sQuery(id+"F2.wireOp",EDGE,"E27.0");var subQ1=sQuery(id+"F2.wireOp",EDGE,"E18.0");var subQ2=makeQuery(id+"F2.imprint","INTERSECT",VERTEX,{"derivedFrom":[subQ1,subQ0]});Q114=makeQuery(id+"F2.imprint","IMPRINT",FACE,{"disambiguationData":[TD([[makeQuery(id+"F2.imprint","IMPRINT",EDGE,{"disambiguationData":[TD([[subQ2,-1.0]])],"derivedFrom":subQ1}),-1.0]])]});}
            var Q115;
            {var subQ0=sQuery(id+"F2.wireOp",EDGE,"E26.0");var subQ1=sQuery(id+"F2.wireOp",EDGE,"E18.0");var subQ2=makeQuery(id+"F2.imprint","INTERSECT",VERTEX,{"derivedFrom":[subQ1,subQ0]});Q115=makeQuery(id+"F2.imprint","IMPRINT",FACE,{"disambiguationData":[TD([[makeQuery(id+"F2.imprint","IMPRINT",EDGE,{"disambiguationData":[TD([[subQ2,-1.0]])],"derivedFrom":subQ1}),-1.0]])]});}
            var Q116;
            {var subQ0=sQuery(id+"F2.wireOp",EDGE,"E25.0");var subQ1=sQuery(id+"F2.wireOp",EDGE,"E18.0");var subQ2=makeQuery(id+"F2.imprint","INTERSECT",VERTEX,{"derivedFrom":[subQ1,subQ0]});Q116=makeQuery(id+"F2.imprint","IMPRINT",FACE,{"disambiguationData":[TD([[makeQuery(id+"F2.imprint","IMPRINT",EDGE,{"disambiguationData":[TD([[subQ2,-1.0]])],"derivedFrom":subQ1}),-1.0]])]});}
            var Q117;
            {var subQ0=sQuery(id+"F2.wireOp",EDGE,"E24.0");var subQ1=sQuery(id+"F2.wireOp",EDGE,"E18.0");var subQ2=makeQuery(id+"F2.imprint","INTERSECT",VERTEX,{"derivedFrom":[subQ1,subQ0]});Q117=makeQuery(id+"F2.imprint","IMPRINT",FACE,{"disambiguationData":[TD([[makeQuery(id+"F2.imprint","IMPRINT",EDGE,{"disambiguationData":[TD([[subQ2,-1.0]])],"derivedFrom":subQ1}),-1.0]])]});}
            var Q118;
            {var subQ0=sQuery(id+"F2.wireOp",EDGE,"E22");var subQ1=sQuery(id+"F2.wireOp",EDGE,"E18.0");var subQ2=makeQuery(id+"F2.imprint","INTERSECT",VERTEX,{"derivedFrom":[subQ1,subQ0]});Q118=makeQuery(id+"F2.imprint","IMPRINT",FACE,{"disambiguationData":[TD([[makeQuery(id+"F2.imprint","IMPRINT",EDGE,{"disambiguationData":[TD([[subQ2,-1.0]])],"derivedFrom":subQ1}),-1.0]])]});}
            var Q119;
            {var subQ0=sQuery(id+"F2.wireOp",EDGE,"E23");var subQ1=sQuery(id+"F2.wireOp",EDGE,"E18.0");var subQ2=makeQuery(id+"F2.imprint","INTERSECT",VERTEX,{"derivedFrom":[subQ1,subQ0]});Q119=makeQuery(id+"F2.imprint","IMPRINT",FACE,{"disambiguationData":[TD([[makeQuery(id+"F2.imprint","IMPRINT",EDGE,{"disambiguationData":[TD([[subQ2,-1.0]])],"derivedFrom":subQ1}),-1.0]])]});}
            var Q120;
            {var subQ0=sQuery(id+"F2.wireOp",EDGE,"E31.0");var subQ1=sQuery(id+"F2.wireOp",EDGE,"E18.0");var subQ2=makeQuery(id+"F2.imprint","INTERSECT",VERTEX,{"derivedFrom":[subQ1,subQ0]});Q120=makeQuery(id+"F2.imprint","IMPRINT",FACE,{"disambiguationData":[TD([[makeQuery(id+"F2.imprint","IMPRINT",EDGE,{"disambiguationData":[TD([[subQ2,-1.0]])],"derivedFrom":subQ1}),-1.0]])]});}
            var Q121;
            {var subQ0=sQuery(id+"F2.wireOp",EDGE,"E30.0");var subQ1=sQuery(id+"F2.wireOp",EDGE,"E18.0");var subQ2=makeQuery(id+"F2.imprint","INTERSECT",VERTEX,{"derivedFrom":[subQ1,subQ0]});Q121=makeQuery(id+"F2.imprint","IMPRINT",FACE,{"disambiguationData":[TD([[makeQuery(id+"F2.imprint","IMPRINT",EDGE,{"disambiguationData":[TD([[subQ2,-1.0]])],"derivedFrom":subQ1}),-1.0]])]});}
            var Q122;
            {var subQ0=sQuery(id+"F2.wireOp",EDGE,"E32.0");var subQ1=sQuery(id+"F2.wireOp",EDGE,"E18.0");var subQ2=makeQuery(id+"F2.imprint","INTERSECT",VERTEX,{"derivedFrom":[subQ1,subQ0]});Q122=makeQuery(id+"F2.imprint","IMPRINT",FACE,{"disambiguationData":[TD([[makeQuery(id+"F2.imprint","IMPRINT",EDGE,{"disambiguationData":[TD([[subQ2,-1.0]])],"derivedFrom":subQ1}),-1.0]])]});}
            var Q123;
            {var subQ0=sQuery(id+"F2.wireOp",EDGE,"E33.0");var subQ1=sQuery(id+"F2.wireOp",EDGE,"E18.0");var subQ2=makeQuery(id+"F2.imprint","INTERSECT",VERTEX,{"derivedFrom":[subQ1,subQ0]});Q123=makeQuery(id+"F2.imprint","IMPRINT",FACE,{"disambiguationData":[TD([[makeQuery(id+"F2.imprint","IMPRINT",EDGE,{"disambiguationData":[TD([[subQ2,-1.0]])],"derivedFrom":subQ1}),-1.0]])]});}
            var Q124;
            {var subQ0=sQuery(id+"F2.wireOp",EDGE,"E34.0");var subQ1=sQuery(id+"F2.wireOp",EDGE,"E18.0");var subQ2=makeQuery(id+"F2.imprint","INTERSECT",VERTEX,{"derivedFrom":[subQ1,subQ0]});Q124=makeQuery(id+"F2.imprint","IMPRINT",FACE,{"disambiguationData":[TD([[makeQuery(id+"F2.imprint","IMPRINT",EDGE,{"disambiguationData":[TD([[subQ2,-1.0]])],"derivedFrom":subQ1}),-1.0]])]});}
            var Q125;
            {var subQ0=sQuery(id+"F2.wireOp",EDGE,"E18.0");var subQ1=sQuery(id+"F2.wireOp",EDGE,"E7.0");var subQ2=makeQuery(id+"F2.imprint","INTERSECT",VERTEX,{"disambiguationData":[OD(1.0)],"derivedFrom":[subQ1,subQ0]});Q125=makeQuery(id+"F2.imprint","IMPRINT",FACE,{"disambiguationData":[TD([[makeQuery(id+"F2.imprint","IMPRINT",EDGE,{"disambiguationData":[TD([[subQ2,-1.0]])],"derivedFrom":subQ1}),-1.0]])]});}
            var Q126;
            {var subQ0=sQuery(id+"F2.wireOp",EDGE,"E28.0");var subQ1=sQuery(id+"F2.wireOp",EDGE,"E7.0");var subQ2=makeQuery(id+"F2.imprint","INTERSECT",VERTEX,{"disambiguationData":[OD(1.0)],"derivedFrom":[subQ1,subQ0]});Q126=makeQuery(id+"F2.imprint","IMPRINT",FACE,{"disambiguationData":[TD([[makeQuery(id+"F2.imprint","IMPRINT",EDGE,{"disambiguationData":[TD([[subQ2,-1.0]])],"derivedFrom":subQ1}),-1.0]])]});}
            var Q127;
            {var subQ0=sQuery(id+"F2.wireOp",EDGE,"E27.0");var subQ1=sQuery(id+"F2.wireOp",EDGE,"E19.0");var subQ2=makeQuery(id+"F2.imprint","INTERSECT",VERTEX,{"derivedFrom":[subQ1,subQ0]});Q127=makeQuery(id+"F2.imprint","IMPRINT",FACE,{"disambiguationData":[TD([[makeQuery(id+"F2.imprint","IMPRINT",EDGE,{"disambiguationData":[TD([[subQ2,-1.0]])],"derivedFrom":subQ1}),-1.0]])]});}
            var Q128;
            {var subQ0=sQuery(id+"F2.wireOp",EDGE,"E25.0");var subQ1=sQuery(id+"F2.wireOp",EDGE,"E19.0");var subQ2=makeQuery(id+"F2.imprint","INTERSECT",VERTEX,{"derivedFrom":[subQ1,subQ0]});Q128=makeQuery(id+"F2.imprint","IMPRINT",FACE,{"disambiguationData":[TD([[makeQuery(id+"F2.imprint","IMPRINT",EDGE,{"disambiguationData":[TD([[subQ2,-1.0]])],"derivedFrom":subQ1}),-1.0]])]});}
            var Q129;
            {var subQ0=sQuery(id+"F2.wireOp",EDGE,"E22");var subQ1=sQuery(id+"F2.wireOp",EDGE,"E19.0");var subQ2=makeQuery(id+"F2.imprint","INTERSECT",VERTEX,{"derivedFrom":[subQ1,subQ0]});Q129=makeQuery(id+"F2.imprint","IMPRINT",FACE,{"disambiguationData":[TD([[makeQuery(id+"F2.imprint","IMPRINT",EDGE,{"disambiguationData":[TD([[subQ2,-1.0]])],"derivedFrom":subQ1}),-1.0]])]});}
            var Q130;
            {var subQ0=sQuery(id+"F2.wireOp",EDGE,"E31.0");var subQ1=sQuery(id+"F2.wireOp",EDGE,"E19.0");var subQ2=makeQuery(id+"F2.imprint","INTERSECT",VERTEX,{"derivedFrom":[subQ1,subQ0]});Q130=makeQuery(id+"F2.imprint","IMPRINT",FACE,{"disambiguationData":[TD([[makeQuery(id+"F2.imprint","IMPRINT",EDGE,{"disambiguationData":[TD([[subQ2,-1.0]])],"derivedFrom":subQ1}),-1.0]])]});}
            var Q131;
            {var subQ0=sQuery(id+"F2.wireOp",EDGE,"E32.0");var subQ1=sQuery(id+"F2.wireOp",EDGE,"E19.0");var subQ2=makeQuery(id+"F2.imprint","INTERSECT",VERTEX,{"derivedFrom":[subQ1,subQ0]});Q131=makeQuery(id+"F2.imprint","IMPRINT",FACE,{"disambiguationData":[TD([[makeQuery(id+"F2.imprint","IMPRINT",EDGE,{"disambiguationData":[TD([[subQ2,-1.0]])],"derivedFrom":subQ1}),-1.0]])]});}
            var Q132;
            {var subQ0=sQuery(id+"F2.wireOp",EDGE,"E34.0");var subQ1=sQuery(id+"F2.wireOp",EDGE,"E7.0");var subQ2=makeQuery(id+"F2.imprint","INTERSECT",VERTEX,{"disambiguationData":[OD(1.0)],"derivedFrom":[subQ1,subQ0]});Q132=makeQuery(id+"F2.imprint","IMPRINT",FACE,{"disambiguationData":[TD([[makeQuery(id+"F2.imprint","IMPRINT",EDGE,{"disambiguationData":[TD([[subQ2,1.0]])],"derivedFrom":subQ1}),-1.0]])]});}
            var Q133;
            {var subQ0=sQuery(id+"F2.wireOp",EDGE,"E20.0");var subQ1=sQuery(id+"F2.wireOp",EDGE,"E7.0");var subQ2=makeQuery(id+"F2.imprint","INTERSECT",VERTEX,{"disambiguationData":[OD(0.0)],"derivedFrom":[subQ1,subQ0]});Q133=makeQuery(id+"F2.imprint","IMPRINT",FACE,{"disambiguationData":[TD([[makeQuery(id+"F2.imprint","IMPRINT",EDGE,{"disambiguationData":[TD([[subQ2,1.0]])],"derivedFrom":subQ1}),-1.0]])]});}
            var Q134;
            {var subQ0=sQuery(id+"F2.wireOp",EDGE,"E27.0");var subQ1=sQuery(id+"F2.wireOp",EDGE,"E20.0");var subQ2=makeQuery(id+"F2.imprint","INTERSECT",VERTEX,{"derivedFrom":[subQ1,subQ0]});Q134=makeQuery(id+"F2.imprint","IMPRINT",FACE,{"disambiguationData":[TD([[makeQuery(id+"F2.imprint","IMPRINT",EDGE,{"disambiguationData":[TD([[subQ2,-1.0]])],"derivedFrom":subQ1}),-1.0]])]});}
            var Q135;
            {var subQ0=sQuery(id+"F2.wireOp",EDGE,"E26.0");var subQ1=sQuery(id+"F2.wireOp",EDGE,"E20.0");var subQ2=makeQuery(id+"F2.imprint","INTERSECT",VERTEX,{"derivedFrom":[subQ1,subQ0]});Q135=makeQuery(id+"F2.imprint","IMPRINT",FACE,{"disambiguationData":[TD([[makeQuery(id+"F2.imprint","IMPRINT",EDGE,{"disambiguationData":[TD([[subQ2,-1.0]])],"derivedFrom":subQ1}),-1.0]])]});}
            var Q136;
            {var subQ0=sQuery(id+"F2.wireOp",EDGE,"E25.0");var subQ1=sQuery(id+"F2.wireOp",EDGE,"E20.0");var subQ2=makeQuery(id+"F2.imprint","INTERSECT",VERTEX,{"derivedFrom":[subQ1,subQ0]});Q136=makeQuery(id+"F2.imprint","IMPRINT",FACE,{"disambiguationData":[TD([[makeQuery(id+"F2.imprint","IMPRINT",EDGE,{"disambiguationData":[TD([[subQ2,-1.0]])],"derivedFrom":subQ1}),-1.0]])]});}
            var Q137;
            {var subQ0=sQuery(id+"F2.wireOp",EDGE,"E24.0");var subQ1=sQuery(id+"F2.wireOp",EDGE,"E20.0");var subQ2=makeQuery(id+"F2.imprint","INTERSECT",VERTEX,{"derivedFrom":[subQ1,subQ0]});Q137=makeQuery(id+"F2.imprint","IMPRINT",FACE,{"disambiguationData":[TD([[makeQuery(id+"F2.imprint","IMPRINT",EDGE,{"disambiguationData":[TD([[subQ2,-1.0]])],"derivedFrom":subQ1}),-1.0]])]});}
            var Q138;
            {var subQ0=sQuery(id+"F2.wireOp",EDGE,"E22");var subQ1=sQuery(id+"F2.wireOp",EDGE,"E20.0");var subQ2=makeQuery(id+"F2.imprint","INTERSECT",VERTEX,{"derivedFrom":[subQ1,subQ0]});Q138=makeQuery(id+"F2.imprint","IMPRINT",FACE,{"disambiguationData":[TD([[makeQuery(id+"F2.imprint","IMPRINT",EDGE,{"disambiguationData":[TD([[subQ2,-1.0]])],"derivedFrom":subQ1}),-1.0]])]});}
            var Q139;
            {var subQ0=sQuery(id+"F2.wireOp",EDGE,"E23");var subQ1=sQuery(id+"F2.wireOp",EDGE,"E20.0");var subQ2=makeQuery(id+"F2.imprint","INTERSECT",VERTEX,{"derivedFrom":[subQ1,subQ0]});Q139=makeQuery(id+"F2.imprint","IMPRINT",FACE,{"disambiguationData":[TD([[makeQuery(id+"F2.imprint","IMPRINT",EDGE,{"disambiguationData":[TD([[subQ2,-1.0]])],"derivedFrom":subQ1}),-1.0]])]});}
            var Q140;
            {var subQ0=sQuery(id+"F2.wireOp",EDGE,"E31.0");var subQ1=sQuery(id+"F2.wireOp",EDGE,"E20.0");var subQ2=makeQuery(id+"F2.imprint","INTERSECT",VERTEX,{"derivedFrom":[subQ1,subQ0]});Q140=makeQuery(id+"F2.imprint","IMPRINT",FACE,{"disambiguationData":[TD([[makeQuery(id+"F2.imprint","IMPRINT",EDGE,{"disambiguationData":[TD([[subQ2,-1.0]])],"derivedFrom":subQ1}),-1.0]])]});}
            var Q141;
            {var subQ0=sQuery(id+"F2.wireOp",EDGE,"E30.0");var subQ1=sQuery(id+"F2.wireOp",EDGE,"E20.0");var subQ2=makeQuery(id+"F2.imprint","INTERSECT",VERTEX,{"derivedFrom":[subQ1,subQ0]});Q141=makeQuery(id+"F2.imprint","IMPRINT",FACE,{"disambiguationData":[TD([[makeQuery(id+"F2.imprint","IMPRINT",EDGE,{"disambiguationData":[TD([[subQ2,-1.0]])],"derivedFrom":subQ1}),-1.0]])]});}
            var Q142;
            {var subQ0=sQuery(id+"F2.wireOp",EDGE,"E32.0");var subQ1=sQuery(id+"F2.wireOp",EDGE,"E20.0");var subQ2=makeQuery(id+"F2.imprint","INTERSECT",VERTEX,{"derivedFrom":[subQ1,subQ0]});Q142=makeQuery(id+"F2.imprint","IMPRINT",FACE,{"disambiguationData":[TD([[makeQuery(id+"F2.imprint","IMPRINT",EDGE,{"disambiguationData":[TD([[subQ2,-1.0]])],"derivedFrom":subQ1}),-1.0]])]});}
            var Q143;
            {var subQ0=sQuery(id+"F2.wireOp",EDGE,"E20.0");var subQ1=sQuery(id+"F2.wireOp",EDGE,"E7.0");var subQ2=makeQuery(id+"F2.imprint","INTERSECT",VERTEX,{"disambiguationData":[OD(1.0)],"derivedFrom":[subQ1,subQ0]});Q143=makeQuery(id+"F2.imprint","IMPRINT",FACE,{"disambiguationData":[TD([[makeQuery(id+"F2.imprint","IMPRINT",EDGE,{"disambiguationData":[TD([[subQ2,-1.0]])],"derivedFrom":subQ1}),-1.0]])]});}
            var Q144;
            {var subQ0=sQuery(id+"F2.wireOp",EDGE,"E26.0");var subQ1=sQuery(id+"F2.wireOp",EDGE,"E7.0");var subQ2=makeQuery(id+"F2.imprint","INTERSECT",VERTEX,{"disambiguationData":[OD(1.0)],"derivedFrom":[subQ1,subQ0]});Q144=makeQuery(id+"F2.imprint","IMPRINT",FACE,{"disambiguationData":[TD([[makeQuery(id+"F2.imprint","IMPRINT",EDGE,{"disambiguationData":[TD([[subQ2,-1.0]])],"derivedFrom":subQ1}),-1.0]])]});}
            var Q145;
            {var subQ0=sQuery(id+"F2.wireOp",EDGE,"E24.0");var subQ1=sQuery(id+"F2.wireOp",EDGE,"E7.0");var subQ2=makeQuery(id+"F2.imprint","INTERSECT",VERTEX,{"disambiguationData":[OD(1.0)],"derivedFrom":[subQ1,subQ0]});Q145=makeQuery(id+"F2.imprint","IMPRINT",FACE,{"disambiguationData":[TD([[makeQuery(id+"F2.imprint","IMPRINT",EDGE,{"disambiguationData":[TD([[subQ2,-1.0]])],"derivedFrom":subQ1}),-1.0]])]});}
            var Q146;
            {var subQ0=sQuery(id+"F2.wireOp",EDGE,"E22");var subQ1=sQuery(id+"F2.wireOp",EDGE,"E7.0");var subQ2=makeQuery(id+"F2.imprint","INTERSECT",VERTEX,{"disambiguationData":[OD(1.0)],"derivedFrom":[subQ1,subQ0]});Q146=makeQuery(id+"F2.imprint","IMPRINT",FACE,{"disambiguationData":[TD([[makeQuery(id+"F2.imprint","IMPRINT",EDGE,{"disambiguationData":[TD([[subQ2,1.0]])],"derivedFrom":subQ1}),-1.0]])]});}
            var Q147;
            {var subQ0=sQuery(id+"F2.wireOp",EDGE,"E30.0");var subQ1=sQuery(id+"F2.wireOp",EDGE,"E7.0");var subQ2=makeQuery(id+"F2.imprint","INTERSECT",VERTEX,{"disambiguationData":[OD(1.0)],"derivedFrom":[subQ1,subQ0]});Q147=makeQuery(id+"F2.imprint","IMPRINT",FACE,{"disambiguationData":[TD([[makeQuery(id+"F2.imprint","IMPRINT",EDGE,{"disambiguationData":[TD([[subQ2,-1.0]])],"derivedFrom":subQ1}),-1.0]])]});}
            var Q148;
            {var subQ0=sQuery(id+"F2.wireOp",EDGE,"E32.0");var subQ1=sQuery(id+"F2.wireOp",EDGE,"E7.0");var subQ2=makeQuery(id+"F2.imprint","INTERSECT",VERTEX,{"disambiguationData":[OD(1.0)],"derivedFrom":[subQ1,subQ0]});Q148=makeQuery(id+"F2.imprint","IMPRINT",FACE,{"disambiguationData":[TD([[makeQuery(id+"F2.imprint","IMPRINT",EDGE,{"disambiguationData":[TD([[subQ2,1.0]])],"derivedFrom":subQ1}),-1.0]])]});}
            extrude(context, id + "F3", {"entities" : qUnion([Q0, Q1, Q2, Q3, Q4, Q5, Q6, Q7, Q8, Q9, Q10, Q11, Q12, Q13, Q14, Q15, Q16, Q17, Q18, Q19, Q20, Q21, Q22, Q23, Q24, Q25, Q26, Q27, Q28, Q29, Q30, Q31, Q32, Q33, Q34, Q35, Q36, Q37, Q38, Q39, Q40, Q41, Q42, Q43, Q44, Q45, Q46, Q47, Q48, Q49, Q50, Q51, Q52, Q53, Q54, Q55, Q56, Q57, Q58, Q59, Q60, Q61, Q62, Q63, Q64, Q65, Q66, Q67, Q68, Q69, Q70, Q71, Q72, Q73, Q74, Q75, Q76, Q77, Q78, Q79, Q80, Q81, Q82, Q83, Q84, Q85, Q86, Q87, Q88, Q89, Q90, Q91, Q92, Q93, Q94, Q95, Q96, Q97, Q98, Q99, Q100, Q101, Q102, Q103, Q104, Q105, Q106, Q107, Q108, Q109, Q110, Q111, Q112, Q113, Q114, Q115, Q116, Q117, Q118, Q119, Q120, Q121, Q122, Q123, Q124, Q125, Q126, Q127, Q128, Q129, Q130, Q131, Q132, Q133, Q134, Q135, Q136, Q137, Q138, Q139, Q140, Q141, Q142, Q143, Q144, Q145, Q146, Q147, Q148]), "operationType" : NewBodyOperationType.ADD, "depth" : 8 * mm, "offsetDistance" : 25 * mm, "hasDraft" : true, "draftAngle" : 5 * degree, "draftPullDirection" : true});
        }
        {
            var Q0;
            Q0=qCreatedBy(makeId("Top.planeOp"),FACE);
            var sketch = newSketch(context, id + "F4", { "sketchPlane" : qUnion([Q0])});
            skCircle(sketch, "E36", {"center": v(0, 0) * mm, "radius": 30 * mm});
            skCircle(sketch, "E37", {"center": v(0, 0) * mm, "radius": 29.5 * mm});
            skLineSegment(sketch, "E38", {"start": v(29.07, 5) * mm, "end": v(29.58, 5) * mm});
            skLineSegment(sketch, "E39", {"start": v(29.07, -5) * mm, "end": v(29.58, -5) * mm});
            skLineSegment(sketch, "E40", {"start": v(0, 0) * mm, "end": v(-30, 0) * mm, "construction": true});
            skLineSegment(sketch, "E41", {"start": v(-15, 25.98) * mm, "end": v(0, 0) * mm, "construction": true});
            skLineSegment(sketch, "E42", {"start": v(15, 25.98) * mm, "end": v(0, 0) * mm, "construction": true});
            skLineSegment(sketch, "E43", {"start": v(15, -25.98) * mm, "end": v(0, 0) * mm, "construction": true});
            skLineSegment(sketch, "E44", {"start": v(-15, -25.98) * mm, "end": v(0, 0) * mm, "construction": true});
            skLineSegment(sketch, "E45", {"start": v(-19.12, 23.12) * mm, "end": v(-18.87, 22.68) * mm});
            skLineSegment(sketch, "E46", {"start": v(-10.46, 28.12) * mm, "end": v(-10.2, 27.68) * mm});
            skLineSegment(sketch, "E47", {"start": v(10.46, 28.12) * mm, "end": v(10.2, 27.68) * mm});
            skLineSegment(sketch, "E48", {"start": v(19.12, 23.12) * mm, "end": v(18.87, 22.68) * mm});
            skLineSegment(sketch, "E49", {"start": v(-19.12, -23.12) * mm, "end": v(-18.87, -22.68) * mm});
            skLineSegment(sketch, "E50", {"start": v(-10.46, -28.12) * mm, "end": v(-10.2, -27.68) * mm});
            skLineSegment(sketch, "E51", {"start": v(10.46, -28.12) * mm, "end": v(10.2, -27.68) * mm});
            skLineSegment(sketch, "E52", {"start": v(19.12, -23.12) * mm, "end": v(18.87, -22.68) * mm});
            skLineSegment(sketch, "E53", {"start": v(-29.58, 5) * mm, "end": v(-29.07, 5) * mm});
            skLineSegment(sketch, "E54", {"start": v(-29.58, -5) * mm, "end": v(-29.07, -5) * mm});
            skSolve(sketch);
        }
        {
            var Q0;
            {var subQ0=sQuery(id+"F4.wireOp",EDGE,"E38");Q0=makeQuery(id+"F4.imprint","IMPRINT",FACE,{"disambiguationData":[TD([[makeQuery(id+"F4.imprint","IMPRINT",EDGE,{"derivedFrom":subQ0}),-1.0]])]});}
            var Q1;
            {var subQ0=sQuery(id+"F4.wireOp",EDGE,"E47");Q1=makeQuery(id+"F4.imprint","IMPRINT",FACE,{"disambiguationData":[TD([[makeQuery(id+"F4.imprint","IMPRINT",EDGE,{"derivedFrom":subQ0}),1.0]])]});}
            var Q2;
            {var subQ0=sQuery(id+"F4.wireOp",EDGE,"E45");Q2=makeQuery(id+"F4.imprint","IMPRINT",FACE,{"disambiguationData":[TD([[makeQuery(id+"F4.imprint","IMPRINT",EDGE,{"derivedFrom":subQ0}),1.0]])]});}
            var Q3;
            {var subQ0=sQuery(id+"F4.wireOp",EDGE,"E53");Q3=makeQuery(id+"F4.imprint","IMPRINT",FACE,{"disambiguationData":[TD([[makeQuery(id+"F4.imprint","IMPRINT",EDGE,{"derivedFrom":subQ0}),-1.0]])]});}
            var Q4;
            {var subQ0=sQuery(id+"F4.wireOp",EDGE,"E49");Q4=makeQuery(id+"F4.imprint","IMPRINT",FACE,{"disambiguationData":[TD([[makeQuery(id+"F4.imprint","IMPRINT",EDGE,{"derivedFrom":subQ0}),-1.0]])]});}
            var Q5;
            {var subQ0=sQuery(id+"F4.wireOp",EDGE,"E51");Q5=makeQuery(id+"F4.imprint","IMPRINT",FACE,{"disambiguationData":[TD([[makeQuery(id+"F4.imprint","IMPRINT",EDGE,{"derivedFrom":subQ0}),-1.0]])]});}
            extrude(context, id + "F5", {"entities" : qUnion([Q0, Q1, Q2, Q3, Q4, Q5]), "operationType" : NewBodyOperationType.ADD, "depth" : 15 * mm, "offsetDistance" : 25 * mm, "hasDraft" : true, "draftAngle" : 5.5 * degree});
        }
        {
            var Q0;
            Q0=qCreatedBy(makeId("Front.planeOp"),FACE);
            var sketch = newSketch(context, id + "F6", { "sketchPlane" : qUnion([Q0])});
            skLineSegment(sketch, "E55.0", {"start": v(28.5, 8) * mm, "end": v(30.5, 4) * mm});
            skLineSegment(sketch, "E56", {"start": v(28.5, 8) * mm, "end": v(25.95, 13.1) * mm});
            skLineSegment(sketch, "E57", {"start": v(25.95, 13.1) * mm, "end": v(25.95, 15.1) * mm});
            skLineSegment(sketch, "E58", {"start": v(25.95, 15.1) * mm, "end": v(29.95, 15.1) * mm});
            skLineSegment(sketch, "E59.0", {"start": v(28.21, 7.43) * mm, "end": v(28.78, 7.43) * mm});
            skLineSegment(sketch, "E60", {"start": v(28.78, 7.43) * mm, "end": v(29.2, 7.43) * mm});
            skLineSegment(sketch, "E61", {"start": v(31.45, 15.1) * mm, "end": v(30.4, 4.2) * mm});
            skLineSegment(sketch, "E62", {"start": v(29.2, 7.43) * mm, "end": v(29.95, 15.1) * mm});
            skSolve(sketch);
        }
        {
            var Q0;
            {var subQ0=sQuery(id+"F6.wireOp",EDGE,"E56");Q0=makeQuery(id+"F6.imprint","IMPRINT",FACE,{"disambiguationData":[TD([[makeQuery(id+"F6.imprint","IMPRINT",EDGE,{"derivedFrom":subQ0}),-1.0]])]});}
            var Q1;
            Q1=makeQuery(id+"F1.opRevolve","SWEPT_FACE",FACE,{"disambiguationData":[OSD([sQuery(id+"F0.wireOp",EDGE,"E3")])]});
            revolve(context, id + "F7", {"operationType" : NewBodyOperationType.REMOVE, "surfaceOperationType" : NewSurfaceOperationType.NEW, "entities" : qUnion([Q0]), "axis" : qUnion([Q1]), "revolveType" : RevolveType.FULL, "oppositeDirection" : true});
        }
    });
